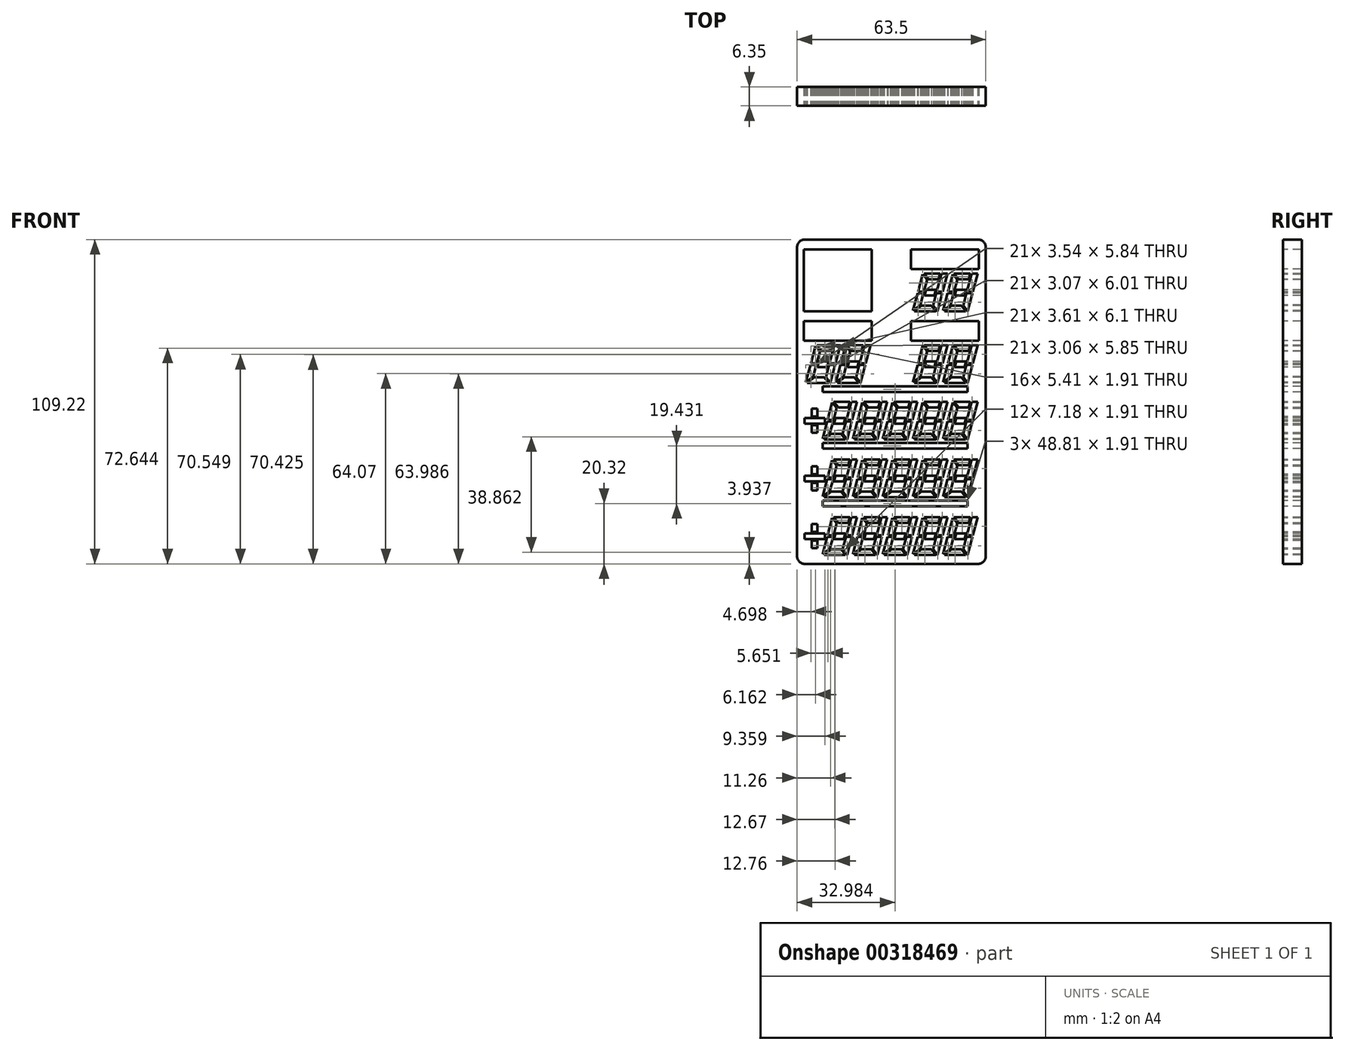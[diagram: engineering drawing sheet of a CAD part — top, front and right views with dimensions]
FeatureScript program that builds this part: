
annotation { "Feature Type Name" : "Feature", "Feature Type Description" : "" }
export const myFeature = defineFeature(function(context is Context, id is Id, definition is map)
    precondition{}
    {
        {
            var Q0;
            Q0=qCreatedBy(makeId("Front.planeOp"),FACE);
            var sketch = newSketch(context, id + "F0", { "sketchPlane" : qUnion([Q0])});
            skLineSegment(sketch, "E0.bottom", {"start": v(31.75, -54.61) * mm, "end": v(-31.75, -54.61) * mm});
            skLineSegment(sketch, "E0.top", {"start": v(31.75, 54.61) * mm, "end": v(-31.75, 54.6) * mm});
            skLineSegment(sketch, "E0.left", {"start": v(31.75, -54.61) * mm, "end": v(31.75, 54.61) * mm});
            skLineSegment(sketch, "E0.right", {"start": v(-31.75, -54.61) * mm, "end": v(-31.75, 54.6) * mm});
            skPoint(sketch, "E0.middle", {"position": v(0, 0) * mm});
            skSolve(sketch);
        }
        {
            var Q0;
            Q0=qSketchRegion(id+"F0",true);
            extrude(context, id + "F1", {"entities" : qUnion([Q0]), "depth" : 6.35 * mm, "offsetDistance" : 25.4 * mm});
        }
        {
            var Q0;
            Q0=makeQuery(id+"F1.opExtrude","CAP_FACE",FACE,{"disambiguationData":[OSD([sQuery(id+"F0.wireOp",EDGE,"E0.bottom"),sQuery(id+"F0.wireOp",EDGE,"E0.top"),sQuery(id+"F0.wireOp",EDGE,"E0.left"),sQuery(id+"F0.wireOp",EDGE,"E0.right")])],"isStart":false});
            var sketch = newSketch(context, id + "F2", { "sketchPlane" : qUnion([Q0])});
            skLineSegment(sketch, "E1", {"start": v(21.11, -38.93) * mm, "end": v(26.52, -38.93) * mm});
            skLineSegment(sketch, "E2", {"start": v(26.52, -38.93) * mm, "end": v(26.01, -40.83) * mm});
            skLineSegment(sketch, "E3", {"start": v(26.01, -40.83) * mm, "end": v(22.7, -40.83) * mm});
            skLineSegment(sketch, "E4", {"start": v(22.7, -40.83) * mm, "end": v(21.11, -38.93) * mm});
            skLineSegment(sketch, "E5", {"start": v(27.05, -38.93) * mm, "end": v(29.02, -38.93) * mm});
            skLineSegment(sketch, "E6", {"start": v(29.02, -38.93) * mm, "end": v(27.39, -45.02) * mm});
            skLineSegment(sketch, "E7", {"start": v(27.05, -38.93) * mm, "end": v(25.41, -45.02) * mm});
            skLineSegment(sketch, "E8", {"start": v(25.41, -45.02) * mm, "end": v(27.39, -45.02) * mm});
            skLineSegment(sketch, "E9", {"start": v(25.28, -45.53) * mm, "end": v(27.25, -45.53) * mm});
            skLineSegment(sketch, "E10", {"start": v(27.25, -45.53) * mm, "end": v(25.64, -51.54) * mm});
            skLineSegment(sketch, "E11", {"start": v(20.65, -39.17) * mm, "end": v(22.15, -40.95) * mm});
            skLineSegment(sketch, "E12", {"start": v(22.15, -40.95) * mm, "end": v(21.06, -45.02) * mm});
            skLineSegment(sketch, "E13", {"start": v(21.06, -45.02) * mm, "end": v(19.09, -45.02) * mm});
            skLineSegment(sketch, "E14", {"start": v(19.09, -45.02) * mm, "end": v(20.65, -39.17) * mm});
            skLineSegment(sketch, "E15", {"start": v(25.28, -45.53) * mm, "end": v(24.18, -49.61) * mm});
            skLineSegment(sketch, "E16", {"start": v(24.18, -49.61) * mm, "end": v(25.64, -51.54) * mm});
            skLineSegment(sketch, "E17", {"start": v(25.06, -51.63) * mm, "end": v(23.63, -49.72) * mm});
            skLineSegment(sketch, "E18", {"start": v(23.63, -49.72) * mm, "end": v(20.33, -49.72) * mm});
            skLineSegment(sketch, "E19", {"start": v(25.06, -51.63) * mm, "end": v(17.89, -51.63) * mm});
            skLineSegment(sketch, "E20", {"start": v(17.89, -51.63) * mm, "end": v(20.33, -49.72) * mm});
            skLineSegment(sketch, "E21", {"start": v(20.92, -45.53) * mm, "end": v(18.95, -45.53) * mm});
            skLineSegment(sketch, "E22", {"start": v(18.95, -45.53) * mm, "end": v(17.39, -51.37) * mm});
            skLineSegment(sketch, "E23", {"start": v(17.39, -51.37) * mm, "end": v(19.88, -49.42) * mm});
            skLineSegment(sketch, "E24", {"start": v(19.88, -49.42) * mm, "end": v(20.92, -45.53) * mm});
            skLineSegment(sketch, "E25", {"start": v(21.77, -44.32) * mm, "end": v(21.26, -46.23) * mm});
            skLineSegment(sketch, "E26", {"start": v(21.26, -46.23) * mm, "end": v(24.56, -46.23) * mm});
            skLineSegment(sketch, "E27", {"start": v(24.56, -46.23) * mm, "end": v(25.08, -44.32) * mm});
            skLineSegment(sketch, "E28", {"start": v(25.08, -44.32) * mm, "end": v(21.77, -44.32) * mm});
            skLineSegment(sketch, "E29.0.1.0", {"start": v(21.26, -26.8) * mm, "end": v(24.56, -26.8) * mm});
            skLineSegment(sketch, "E29.0.1.1", {"start": v(18.95, -26.1) * mm, "end": v(17.39, -31.94) * mm});
            skLineSegment(sketch, "E29.0.1.2", {"start": v(22.15, -21.52) * mm, "end": v(21.06, -25.6) * mm});
            skLineSegment(sketch, "E29.0.1.3", {"start": v(29.02, -19.5) * mm, "end": v(27.39, -25.6) * mm});
            skLineSegment(sketch, "E29.0.1.4", {"start": v(26.01, -21.4) * mm, "end": v(22.7, -21.4) * mm});
            skLineSegment(sketch, "E29.0.1.5", {"start": v(25.06, -32.2) * mm, "end": v(17.89, -32.2) * mm});
            skLineSegment(sketch, "E29.0.1.6", {"start": v(27.05, -19.5) * mm, "end": v(25.41, -25.6) * mm});
            skLineSegment(sketch, "E29.0.1.7", {"start": v(23.63, -30.29) * mm, "end": v(20.33, -30.29) * mm});
            skLineSegment(sketch, "E29.0.1.8", {"start": v(25.08, -24.9) * mm, "end": v(21.77, -24.9) * mm});
            skLineSegment(sketch, "E29.0.1.9", {"start": v(25.28, -26.1) * mm, "end": v(24.18, -30.18) * mm});
            skLineSegment(sketch, "E29.0.1.10", {"start": v(27.25, -26.1) * mm, "end": v(25.64, -32.11) * mm});
            skLineSegment(sketch, "E29.0.1.11", {"start": v(19.09, -25.6) * mm, "end": v(20.65, -19.74) * mm});
            skLineSegment(sketch, "E29.0.1.12", {"start": v(21.11, -19.5) * mm, "end": v(26.52, -19.5) * mm});
            skLineSegment(sketch, "E29.0.1.13", {"start": v(20.65, -19.74) * mm, "end": v(22.15, -21.52) * mm});
            skLineSegment(sketch, "E29.0.1.14", {"start": v(21.06, -25.6) * mm, "end": v(19.09, -25.6) * mm});
            skLineSegment(sketch, "E29.0.1.15", {"start": v(19.88, -30) * mm, "end": v(20.92, -26.1) * mm});
            skLineSegment(sketch, "E29.0.1.16", {"start": v(22.7, -21.4) * mm, "end": v(21.11, -19.5) * mm});
            skLineSegment(sketch, "E29.0.1.17", {"start": v(17.89, -32.2) * mm, "end": v(20.33, -30.29) * mm});
            skLineSegment(sketch, "E29.0.1.18", {"start": v(27.05, -19.5) * mm, "end": v(29.02, -19.5) * mm});
            skLineSegment(sketch, "E29.0.1.19", {"start": v(20.92, -26.1) * mm, "end": v(18.95, -26.1) * mm});
            skLineSegment(sketch, "E29.0.1.20", {"start": v(17.39, -31.94) * mm, "end": v(19.88, -30) * mm});
            skLineSegment(sketch, "E29.0.1.21", {"start": v(25.06, -32.2) * mm, "end": v(23.63, -30.29) * mm});
            skLineSegment(sketch, "E29.0.1.22", {"start": v(26.52, -19.5) * mm, "end": v(26.01, -21.4) * mm});
            skLineSegment(sketch, "E29.0.1.23", {"start": v(24.18, -30.18) * mm, "end": v(25.64, -32.11) * mm});
            skLineSegment(sketch, "E29.0.1.24", {"start": v(21.77, -24.9) * mm, "end": v(21.26, -26.8) * mm});
            skLineSegment(sketch, "E29.0.1.25", {"start": v(25.28, -26.1) * mm, "end": v(27.25, -26.1) * mm});
            skLineSegment(sketch, "E29.0.1.26", {"start": v(25.41, -25.6) * mm, "end": v(27.39, -25.6) * mm});
            skLineSegment(sketch, "E29.0.1.27", {"start": v(24.56, -26.8) * mm, "end": v(25.08, -24.9) * mm});
            skLineSegment(sketch, "E29.0.2.0", {"start": v(21.26, -7.37) * mm, "end": v(24.56, -7.37) * mm});
            skLineSegment(sketch, "E29.0.2.1", {"start": v(18.95, -6.67) * mm, "end": v(17.39, -12.51) * mm});
            skLineSegment(sketch, "E29.0.2.2", {"start": v(22.15, -2.1) * mm, "end": v(21.06, -6.16) * mm});
            skLineSegment(sketch, "E29.0.2.3", {"start": v(29.02, -0.06) * mm, "end": v(27.39, -6.16) * mm});
            skLineSegment(sketch, "E29.0.2.4", {"start": v(26.01, -1.97) * mm, "end": v(22.7, -1.97) * mm});
            skLineSegment(sketch, "E29.0.2.5", {"start": v(25.06, -12.76) * mm, "end": v(17.89, -12.76) * mm});
            skLineSegment(sketch, "E29.0.2.6", {"start": v(27.05, -0.06) * mm, "end": v(25.41, -6.16) * mm});
            skLineSegment(sketch, "E29.0.2.7", {"start": v(23.63, -10.86) * mm, "end": v(20.33, -10.86) * mm});
            skLineSegment(sketch, "E29.0.2.8", {"start": v(25.08, -5.46) * mm, "end": v(21.77, -5.46) * mm});
            skLineSegment(sketch, "E29.0.2.9", {"start": v(25.28, -6.67) * mm, "end": v(24.18, -10.75) * mm});
            skLineSegment(sketch, "E29.0.2.10", {"start": v(27.25, -6.67) * mm, "end": v(25.64, -12.68) * mm});
            skLineSegment(sketch, "E29.0.2.11", {"start": v(19.09, -6.16) * mm, "end": v(20.65, -0.31) * mm});
            skLineSegment(sketch, "E29.0.2.12", {"start": v(21.11, -0.06) * mm, "end": v(26.52, -0.06) * mm});
            skLineSegment(sketch, "E29.0.2.13", {"start": v(20.65, -0.31) * mm, "end": v(22.15, -2.1) * mm});
            skLineSegment(sketch, "E29.0.2.14", {"start": v(21.06, -6.16) * mm, "end": v(19.09, -6.16) * mm});
            skLineSegment(sketch, "E29.0.2.15", {"start": v(19.88, -10.56) * mm, "end": v(20.92, -6.67) * mm});
            skLineSegment(sketch, "E29.0.2.16", {"start": v(22.7, -1.97) * mm, "end": v(21.11, -0.06) * mm});
            skLineSegment(sketch, "E29.0.2.17", {"start": v(17.89, -12.76) * mm, "end": v(20.33, -10.86) * mm});
            skLineSegment(sketch, "E29.0.2.18", {"start": v(27.05, -0.06) * mm, "end": v(29.02, -0.06) * mm});
            skLineSegment(sketch, "E29.0.2.19", {"start": v(20.92, -6.67) * mm, "end": v(18.95, -6.67) * mm});
            skLineSegment(sketch, "E29.0.2.20", {"start": v(17.39, -12.51) * mm, "end": v(19.88, -10.56) * mm});
            skLineSegment(sketch, "E29.0.2.21", {"start": v(25.06, -12.76) * mm, "end": v(23.63, -10.86) * mm});
            skLineSegment(sketch, "E29.0.2.22", {"start": v(26.52, -0.06) * mm, "end": v(26.01, -1.97) * mm});
            skLineSegment(sketch, "E29.0.2.23", {"start": v(24.18, -10.75) * mm, "end": v(25.64, -12.68) * mm});
            skLineSegment(sketch, "E29.0.2.24", {"start": v(21.77, -5.46) * mm, "end": v(21.26, -7.37) * mm});
            skLineSegment(sketch, "E29.0.2.25", {"start": v(25.28, -6.67) * mm, "end": v(27.25, -6.67) * mm});
            skLineSegment(sketch, "E29.0.2.26", {"start": v(25.41, -6.16) * mm, "end": v(27.39, -6.16) * mm});
            skLineSegment(sketch, "E29.0.2.27", {"start": v(24.56, -7.37) * mm, "end": v(25.08, -5.46) * mm});
            skLineSegment(sketch, "E29.1.0.0", {"start": v(11.12, -46.23) * mm, "end": v(14.43, -46.23) * mm});
            skLineSegment(sketch, "E29.1.0.1", {"start": v(8.81, -45.53) * mm, "end": v(7.25, -51.37) * mm});
            skLineSegment(sketch, "E29.1.0.2", {"start": v(12.01, -40.95) * mm, "end": v(10.92, -45.02) * mm});
            skLineSegment(sketch, "E29.1.0.3", {"start": v(18.88, -38.93) * mm, "end": v(17.25, -45.02) * mm});
            skLineSegment(sketch, "E29.1.0.4", {"start": v(15.87, -40.83) * mm, "end": v(12.57, -40.83) * mm});
            skLineSegment(sketch, "E29.1.0.5", {"start": v(14.93, -51.63) * mm, "end": v(7.75, -51.63) * mm});
            skLineSegment(sketch, "E29.1.0.6", {"start": v(16.9, -38.93) * mm, "end": v(15.27, -45.02) * mm});
            skLineSegment(sketch, "E29.1.0.7", {"start": v(13.49, -49.72) * mm, "end": v(10.19, -49.72) * mm});
            skLineSegment(sketch, "E29.1.0.8", {"start": v(14.94, -44.32) * mm, "end": v(11.63, -44.32) * mm});
            skLineSegment(sketch, "E29.1.0.9", {"start": v(15.14, -45.53) * mm, "end": v(14.04, -49.61) * mm});
            skLineSegment(sketch, "E29.1.0.10", {"start": v(17.11, -45.53) * mm, "end": v(15.5, -51.54) * mm});
            skLineSegment(sketch, "E29.1.0.11", {"start": v(8.95, -45.02) * mm, "end": v(10.52, -39.17) * mm});
            skLineSegment(sketch, "E29.1.0.12", {"start": v(10.97, -38.93) * mm, "end": v(16.38, -38.93) * mm});
            skLineSegment(sketch, "E29.1.0.13", {"start": v(10.52, -39.17) * mm, "end": v(12.01, -40.95) * mm});
            skLineSegment(sketch, "E29.1.0.14", {"start": v(10.92, -45.02) * mm, "end": v(8.95, -45.02) * mm});
            skLineSegment(sketch, "E29.1.0.15", {"start": v(9.74, -49.42) * mm, "end": v(10.78, -45.53) * mm});
            skLineSegment(sketch, "E29.1.0.16", {"start": v(12.57, -40.83) * mm, "end": v(10.97, -38.93) * mm});
            skLineSegment(sketch, "E29.1.0.17", {"start": v(7.75, -51.63) * mm, "end": v(10.19, -49.72) * mm});
            skLineSegment(sketch, "E29.1.0.18", {"start": v(16.9, -38.93) * mm, "end": v(18.88, -38.93) * mm});
            skLineSegment(sketch, "E29.1.0.19", {"start": v(10.78, -45.53) * mm, "end": v(8.81, -45.53) * mm});
            skLineSegment(sketch, "E29.1.0.20", {"start": v(7.25, -51.37) * mm, "end": v(9.74, -49.42) * mm});
            skLineSegment(sketch, "E29.1.0.21", {"start": v(14.93, -51.63) * mm, "end": v(13.49, -49.72) * mm});
            skLineSegment(sketch, "E29.1.0.22", {"start": v(16.38, -38.93) * mm, "end": v(15.87, -40.83) * mm});
            skLineSegment(sketch, "E29.1.0.23", {"start": v(14.04, -49.61) * mm, "end": v(15.5, -51.54) * mm});
            skLineSegment(sketch, "E29.1.0.24", {"start": v(11.63, -44.32) * mm, "end": v(11.12, -46.23) * mm});
            skLineSegment(sketch, "E29.1.0.25", {"start": v(15.14, -45.53) * mm, "end": v(17.11, -45.53) * mm});
            skLineSegment(sketch, "E29.1.0.26", {"start": v(15.27, -45.02) * mm, "end": v(17.25, -45.02) * mm});
            skLineSegment(sketch, "E29.1.0.27", {"start": v(14.43, -46.23) * mm, "end": v(14.94, -44.32) * mm});
            skLineSegment(sketch, "E29.1.1.0", {"start": v(11.12, -26.8) * mm, "end": v(14.43, -26.8) * mm});
            skLineSegment(sketch, "E29.1.1.1", {"start": v(8.81, -26.1) * mm, "end": v(7.25, -31.94) * mm});
            skLineSegment(sketch, "E29.1.1.2", {"start": v(12.01, -21.52) * mm, "end": v(10.92, -25.6) * mm});
            skLineSegment(sketch, "E29.1.1.3", {"start": v(18.88, -19.5) * mm, "end": v(17.25, -25.6) * mm});
            skLineSegment(sketch, "E29.1.1.4", {"start": v(15.87, -21.4) * mm, "end": v(12.57, -21.4) * mm});
            skLineSegment(sketch, "E29.1.1.5", {"start": v(14.93, -32.2) * mm, "end": v(7.75, -32.2) * mm});
            skLineSegment(sketch, "E29.1.1.6", {"start": v(16.9, -19.5) * mm, "end": v(15.27, -25.6) * mm});
            skLineSegment(sketch, "E29.1.1.7", {"start": v(13.49, -30.29) * mm, "end": v(10.19, -30.29) * mm});
            skLineSegment(sketch, "E29.1.1.8", {"start": v(14.94, -24.9) * mm, "end": v(11.63, -24.9) * mm});
            skLineSegment(sketch, "E29.1.1.9", {"start": v(15.14, -26.1) * mm, "end": v(14.04, -30.18) * mm});
            skLineSegment(sketch, "E29.1.1.10", {"start": v(17.11, -26.1) * mm, "end": v(15.5, -32.11) * mm});
            skLineSegment(sketch, "E29.1.1.11", {"start": v(8.95, -25.6) * mm, "end": v(10.52, -19.74) * mm});
            skLineSegment(sketch, "E29.1.1.12", {"start": v(10.97, -19.5) * mm, "end": v(16.38, -19.5) * mm});
            skLineSegment(sketch, "E29.1.1.13", {"start": v(10.52, -19.74) * mm, "end": v(12.01, -21.52) * mm});
            skLineSegment(sketch, "E29.1.1.14", {"start": v(10.92, -25.6) * mm, "end": v(8.95, -25.6) * mm});
            skLineSegment(sketch, "E29.1.1.15", {"start": v(9.74, -30) * mm, "end": v(10.78, -26.1) * mm});
            skLineSegment(sketch, "E29.1.1.16", {"start": v(12.57, -21.4) * mm, "end": v(10.97, -19.5) * mm});
            skLineSegment(sketch, "E29.1.1.17", {"start": v(7.75, -32.2) * mm, "end": v(10.19, -30.29) * mm});
            skLineSegment(sketch, "E29.1.1.18", {"start": v(16.9, -19.5) * mm, "end": v(18.88, -19.5) * mm});
            skLineSegment(sketch, "E29.1.1.19", {"start": v(10.78, -26.1) * mm, "end": v(8.81, -26.1) * mm});
            skLineSegment(sketch, "E29.1.1.20", {"start": v(7.25, -31.94) * mm, "end": v(9.74, -30) * mm});
            skLineSegment(sketch, "E29.1.1.21", {"start": v(14.93, -32.2) * mm, "end": v(13.49, -30.29) * mm});
            skLineSegment(sketch, "E29.1.1.22", {"start": v(16.38, -19.5) * mm, "end": v(15.87, -21.4) * mm});
            skLineSegment(sketch, "E29.1.1.23", {"start": v(14.04, -30.18) * mm, "end": v(15.5, -32.11) * mm});
            skLineSegment(sketch, "E29.1.1.24", {"start": v(11.63, -24.9) * mm, "end": v(11.12, -26.8) * mm});
            skLineSegment(sketch, "E29.1.1.25", {"start": v(15.14, -26.1) * mm, "end": v(17.11, -26.1) * mm});
            skLineSegment(sketch, "E29.1.1.26", {"start": v(15.27, -25.6) * mm, "end": v(17.25, -25.6) * mm});
            skLineSegment(sketch, "E29.1.1.27", {"start": v(14.43, -26.8) * mm, "end": v(14.94, -24.9) * mm});
            skLineSegment(sketch, "E29.1.2.0", {"start": v(11.12, -7.37) * mm, "end": v(14.43, -7.37) * mm});
            skLineSegment(sketch, "E29.1.2.1", {"start": v(8.81, -6.67) * mm, "end": v(7.25, -12.51) * mm});
            skLineSegment(sketch, "E29.1.2.2", {"start": v(12.01, -2.1) * mm, "end": v(10.92, -6.16) * mm});
            skLineSegment(sketch, "E29.1.2.3", {"start": v(18.88, -0.06) * mm, "end": v(17.25, -6.16) * mm});
            skLineSegment(sketch, "E29.1.2.4", {"start": v(15.87, -1.97) * mm, "end": v(12.57, -1.97) * mm});
            skLineSegment(sketch, "E29.1.2.5", {"start": v(14.93, -12.76) * mm, "end": v(7.75, -12.76) * mm});
            skLineSegment(sketch, "E29.1.2.6", {"start": v(16.9, -0.06) * mm, "end": v(15.27, -6.16) * mm});
            skLineSegment(sketch, "E29.1.2.7", {"start": v(13.49, -10.86) * mm, "end": v(10.19, -10.86) * mm});
            skLineSegment(sketch, "E29.1.2.8", {"start": v(14.94, -5.46) * mm, "end": v(11.63, -5.46) * mm});
            skLineSegment(sketch, "E29.1.2.9", {"start": v(15.14, -6.67) * mm, "end": v(14.04, -10.75) * mm});
            skLineSegment(sketch, "E29.1.2.10", {"start": v(17.11, -6.67) * mm, "end": v(15.5, -12.68) * mm});
            skLineSegment(sketch, "E29.1.2.11", {"start": v(8.95, -6.16) * mm, "end": v(10.52, -0.31) * mm});
            skLineSegment(sketch, "E29.1.2.12", {"start": v(10.97, -0.06) * mm, "end": v(16.38, -0.06) * mm});
            skLineSegment(sketch, "E29.1.2.13", {"start": v(10.52, -0.31) * mm, "end": v(12.01, -2.1) * mm});
            skLineSegment(sketch, "E29.1.2.14", {"start": v(10.92, -6.16) * mm, "end": v(8.95, -6.16) * mm});
            skLineSegment(sketch, "E29.1.2.15", {"start": v(9.74, -10.56) * mm, "end": v(10.78, -6.67) * mm});
            skLineSegment(sketch, "E29.1.2.16", {"start": v(12.57, -1.97) * mm, "end": v(10.97, -0.06) * mm});
            skLineSegment(sketch, "E29.1.2.17", {"start": v(7.75, -12.76) * mm, "end": v(10.19, -10.86) * mm});
            skLineSegment(sketch, "E29.1.2.18", {"start": v(16.9, -0.06) * mm, "end": v(18.88, -0.06) * mm});
            skLineSegment(sketch, "E29.1.2.19", {"start": v(10.78, -6.67) * mm, "end": v(8.81, -6.67) * mm});
            skLineSegment(sketch, "E29.1.2.20", {"start": v(7.25, -12.51) * mm, "end": v(9.74, -10.56) * mm});
            skLineSegment(sketch, "E29.1.2.21", {"start": v(14.93, -12.76) * mm, "end": v(13.49, -10.86) * mm});
            skLineSegment(sketch, "E29.1.2.22", {"start": v(16.38, -0.06) * mm, "end": v(15.87, -1.97) * mm});
            skLineSegment(sketch, "E29.1.2.23", {"start": v(14.04, -10.75) * mm, "end": v(15.5, -12.68) * mm});
            skLineSegment(sketch, "E29.1.2.24", {"start": v(11.63, -5.46) * mm, "end": v(11.12, -7.37) * mm});
            skLineSegment(sketch, "E29.1.2.25", {"start": v(15.14, -6.67) * mm, "end": v(17.11, -6.67) * mm});
            skLineSegment(sketch, "E29.1.2.26", {"start": v(15.27, -6.16) * mm, "end": v(17.25, -6.16) * mm});
            skLineSegment(sketch, "E29.1.2.27", {"start": v(14.43, -7.37) * mm, "end": v(14.94, -5.46) * mm});
            skLineSegment(sketch, "E29.2.0.0", {"start": v(0.98, -46.23) * mm, "end": v(4.29, -46.23) * mm});
            skLineSegment(sketch, "E29.2.0.1", {"start": v(-1.33, -45.53) * mm, "end": v(-2.9, -51.37) * mm});
            skLineSegment(sketch, "E29.2.0.2", {"start": v(1.87, -40.95) * mm, "end": v(0.78, -45.02) * mm});
            skLineSegment(sketch, "E29.2.0.3", {"start": v(8.74, -38.93) * mm, "end": v(7.1, -45.02) * mm});
            skLineSegment(sketch, "E29.2.0.4", {"start": v(5.73, -40.83) * mm, "end": v(2.43, -40.83) * mm});
            skLineSegment(sketch, "E29.2.0.5", {"start": v(4.79, -51.63) * mm, "end": v(-2.39, -51.63) * mm});
            skLineSegment(sketch, "E29.2.0.6", {"start": v(6.77, -38.93) * mm, "end": v(5.14, -45.02) * mm});
            skLineSegment(sketch, "E29.2.0.7", {"start": v(3.35, -49.72) * mm, "end": v(0.05, -49.72) * mm});
            skLineSegment(sketch, "E29.2.0.8", {"start": v(4.8, -44.32) * mm, "end": v(1.5, -44.32) * mm});
            skLineSegment(sketch, "E29.2.0.9", {"start": v(5, -45.53) * mm, "end": v(3.9, -49.61) * mm});
            skLineSegment(sketch, "E29.2.0.10", {"start": v(6.97, -45.53) * mm, "end": v(5.36, -51.54) * mm});
            skLineSegment(sketch, "E29.2.0.11", {"start": v(-1.2, -45.02) * mm, "end": v(0.38, -39.17) * mm});
            skLineSegment(sketch, "E29.2.0.12", {"start": v(0.83, -38.93) * mm, "end": v(6.24, -38.93) * mm});
            skLineSegment(sketch, "E29.2.0.13", {"start": v(0.38, -39.17) * mm, "end": v(1.87, -40.95) * mm});
            skLineSegment(sketch, "E29.2.0.14", {"start": v(0.78, -45.02) * mm, "end": v(-1.2, -45.02) * mm});
            skLineSegment(sketch, "E29.2.0.15", {"start": v(-0.4, -49.42) * mm, "end": v(0.65, -45.53) * mm});
            skLineSegment(sketch, "E29.2.0.16", {"start": v(2.43, -40.83) * mm, "end": v(0.83, -38.93) * mm});
            skLineSegment(sketch, "E29.2.0.17", {"start": v(-2.39, -51.63) * mm, "end": v(0.05, -49.72) * mm});
            skLineSegment(sketch, "E29.2.0.18", {"start": v(6.77, -38.93) * mm, "end": v(8.74, -38.93) * mm});
            skLineSegment(sketch, "E29.2.0.19", {"start": v(0.65, -45.53) * mm, "end": v(-1.33, -45.53) * mm});
            skLineSegment(sketch, "E29.2.0.20", {"start": v(-2.9, -51.37) * mm, "end": v(-0.4, -49.42) * mm});
            skLineSegment(sketch, "E29.2.0.21", {"start": v(4.79, -51.63) * mm, "end": v(3.35, -49.72) * mm});
            skLineSegment(sketch, "E29.2.0.22", {"start": v(6.24, -38.93) * mm, "end": v(5.73, -40.83) * mm});
            skLineSegment(sketch, "E29.2.0.23", {"start": v(3.9, -49.61) * mm, "end": v(5.36, -51.54) * mm});
            skLineSegment(sketch, "E29.2.0.24", {"start": v(1.5, -44.32) * mm, "end": v(0.98, -46.23) * mm});
            skLineSegment(sketch, "E29.2.0.25", {"start": v(5, -45.53) * mm, "end": v(6.97, -45.53) * mm});
            skLineSegment(sketch, "E29.2.0.26", {"start": v(5.14, -45.02) * mm, "end": v(7.1, -45.02) * mm});
            skLineSegment(sketch, "E29.2.0.27", {"start": v(4.29, -46.23) * mm, "end": v(4.8, -44.32) * mm});
            skLineSegment(sketch, "E29.2.1.0", {"start": v(0.98, -26.8) * mm, "end": v(4.29, -26.8) * mm});
            skLineSegment(sketch, "E29.2.1.1", {"start": v(-1.33, -26.1) * mm, "end": v(-2.9, -31.94) * mm});
            skLineSegment(sketch, "E29.2.1.2", {"start": v(1.87, -21.52) * mm, "end": v(0.78, -25.6) * mm});
            skLineSegment(sketch, "E29.2.1.3", {"start": v(8.74, -19.5) * mm, "end": v(7.1, -25.6) * mm});
            skLineSegment(sketch, "E29.2.1.4", {"start": v(5.73, -21.4) * mm, "end": v(2.43, -21.4) * mm});
            skLineSegment(sketch, "E29.2.1.5", {"start": v(4.79, -32.2) * mm, "end": v(-2.39, -32.2) * mm});
            skLineSegment(sketch, "E29.2.1.6", {"start": v(6.77, -19.5) * mm, "end": v(5.14, -25.6) * mm});
            skLineSegment(sketch, "E29.2.1.7", {"start": v(3.35, -30.29) * mm, "end": v(0.05, -30.29) * mm});
            skLineSegment(sketch, "E29.2.1.8", {"start": v(4.8, -24.9) * mm, "end": v(1.5, -24.9) * mm});
            skLineSegment(sketch, "E29.2.1.9", {"start": v(5, -26.1) * mm, "end": v(3.9, -30.18) * mm});
            skLineSegment(sketch, "E29.2.1.10", {"start": v(6.97, -26.1) * mm, "end": v(5.36, -32.11) * mm});
            skLineSegment(sketch, "E29.2.1.11", {"start": v(-1.2, -25.6) * mm, "end": v(0.38, -19.74) * mm});
            skLineSegment(sketch, "E29.2.1.12", {"start": v(0.83, -19.5) * mm, "end": v(6.24, -19.5) * mm});
            skLineSegment(sketch, "E29.2.1.13", {"start": v(0.38, -19.74) * mm, "end": v(1.87, -21.52) * mm});
            skLineSegment(sketch, "E29.2.1.14", {"start": v(0.78, -25.6) * mm, "end": v(-1.2, -25.6) * mm});
            skLineSegment(sketch, "E29.2.1.15", {"start": v(-0.4, -30) * mm, "end": v(0.65, -26.1) * mm});
            skLineSegment(sketch, "E29.2.1.16", {"start": v(2.43, -21.4) * mm, "end": v(0.83, -19.5) * mm});
            skLineSegment(sketch, "E29.2.1.17", {"start": v(-2.39, -32.2) * mm, "end": v(0.05, -30.29) * mm});
            skLineSegment(sketch, "E29.2.1.18", {"start": v(6.77, -19.5) * mm, "end": v(8.74, -19.5) * mm});
            skLineSegment(sketch, "E29.2.1.19", {"start": v(0.65, -26.1) * mm, "end": v(-1.33, -26.1) * mm});
            skLineSegment(sketch, "E29.2.1.20", {"start": v(-2.9, -31.94) * mm, "end": v(-0.4, -30) * mm});
            skLineSegment(sketch, "E29.2.1.21", {"start": v(4.79, -32.2) * mm, "end": v(3.35, -30.29) * mm});
            skLineSegment(sketch, "E29.2.1.22", {"start": v(6.24, -19.5) * mm, "end": v(5.73, -21.4) * mm});
            skLineSegment(sketch, "E29.2.1.23", {"start": v(3.9, -30.18) * mm, "end": v(5.36, -32.11) * mm});
            skLineSegment(sketch, "E29.2.1.24", {"start": v(1.5, -24.9) * mm, "end": v(0.98, -26.8) * mm});
            skLineSegment(sketch, "E29.2.1.25", {"start": v(5, -26.1) * mm, "end": v(6.97, -26.1) * mm});
            skLineSegment(sketch, "E29.2.1.26", {"start": v(5.14, -25.6) * mm, "end": v(7.1, -25.6) * mm});
            skLineSegment(sketch, "E29.2.1.27", {"start": v(4.29, -26.8) * mm, "end": v(4.8, -24.9) * mm});
            skLineSegment(sketch, "E29.2.2.0", {"start": v(0.98, -7.37) * mm, "end": v(4.29, -7.37) * mm});
            skLineSegment(sketch, "E29.2.2.1", {"start": v(-1.33, -6.67) * mm, "end": v(-2.9, -12.51) * mm});
            skLineSegment(sketch, "E29.2.2.2", {"start": v(1.87, -2.1) * mm, "end": v(0.78, -6.16) * mm});
            skLineSegment(sketch, "E29.2.2.3", {"start": v(8.74, -0.06) * mm, "end": v(7.1, -6.16) * mm});
            skLineSegment(sketch, "E29.2.2.4", {"start": v(5.73, -1.97) * mm, "end": v(2.43, -1.97) * mm});
            skLineSegment(sketch, "E29.2.2.5", {"start": v(4.79, -12.76) * mm, "end": v(-2.39, -12.76) * mm});
            skLineSegment(sketch, "E29.2.2.6", {"start": v(6.77, -0.06) * mm, "end": v(5.14, -6.16) * mm});
            skLineSegment(sketch, "E29.2.2.7", {"start": v(3.35, -10.86) * mm, "end": v(0.05, -10.86) * mm});
            skLineSegment(sketch, "E29.2.2.8", {"start": v(4.8, -5.46) * mm, "end": v(1.5, -5.46) * mm});
            skLineSegment(sketch, "E29.2.2.9", {"start": v(5, -6.67) * mm, "end": v(3.9, -10.75) * mm});
            skLineSegment(sketch, "E29.2.2.10", {"start": v(6.97, -6.67) * mm, "end": v(5.36, -12.68) * mm});
            skLineSegment(sketch, "E29.2.2.11", {"start": v(-1.2, -6.16) * mm, "end": v(0.38, -0.31) * mm});
            skLineSegment(sketch, "E29.2.2.12", {"start": v(0.83, -0.06) * mm, "end": v(6.24, -0.06) * mm});
            skLineSegment(sketch, "E29.2.2.13", {"start": v(0.38, -0.31) * mm, "end": v(1.87, -2.1) * mm});
            skLineSegment(sketch, "E29.2.2.14", {"start": v(0.78, -6.16) * mm, "end": v(-1.2, -6.16) * mm});
            skLineSegment(sketch, "E29.2.2.15", {"start": v(-0.4, -10.56) * mm, "end": v(0.65, -6.67) * mm});
            skLineSegment(sketch, "E29.2.2.16", {"start": v(2.43, -1.97) * mm, "end": v(0.83, -0.06) * mm});
            skLineSegment(sketch, "E29.2.2.17", {"start": v(-2.39, -12.76) * mm, "end": v(0.05, -10.86) * mm});
            skLineSegment(sketch, "E29.2.2.18", {"start": v(6.77, -0.06) * mm, "end": v(8.74, -0.06) * mm});
            skLineSegment(sketch, "E29.2.2.19", {"start": v(0.65, -6.67) * mm, "end": v(-1.33, -6.67) * mm});
            skLineSegment(sketch, "E29.2.2.20", {"start": v(-2.9, -12.51) * mm, "end": v(-0.4, -10.56) * mm});
            skLineSegment(sketch, "E29.2.2.21", {"start": v(4.79, -12.76) * mm, "end": v(3.35, -10.86) * mm});
            skLineSegment(sketch, "E29.2.2.22", {"start": v(6.24, -0.06) * mm, "end": v(5.73, -1.97) * mm});
            skLineSegment(sketch, "E29.2.2.23", {"start": v(3.9, -10.75) * mm, "end": v(5.36, -12.68) * mm});
            skLineSegment(sketch, "E29.2.2.24", {"start": v(1.5, -5.46) * mm, "end": v(0.98, -7.37) * mm});
            skLineSegment(sketch, "E29.2.2.25", {"start": v(5, -6.67) * mm, "end": v(6.97, -6.67) * mm});
            skLineSegment(sketch, "E29.2.2.26", {"start": v(5.14, -6.16) * mm, "end": v(7.1, -6.16) * mm});
            skLineSegment(sketch, "E29.2.2.27", {"start": v(4.29, -7.37) * mm, "end": v(4.8, -5.46) * mm});
            skLineSegment(sketch, "E29.3.0.0", {"start": v(-9.15, -46.23) * mm, "end": v(-5.85, -46.23) * mm});
            skLineSegment(sketch, "E29.3.0.1", {"start": v(-11.47, -45.53) * mm, "end": v(-13.03, -51.37) * mm});
            skLineSegment(sketch, "E29.3.0.2", {"start": v(-8.27, -40.95) * mm, "end": v(-9.36, -45.02) * mm});
            skLineSegment(sketch, "E29.3.0.3", {"start": v(-1.4, -38.93) * mm, "end": v(-3.03, -45.02) * mm});
            skLineSegment(sketch, "E29.3.0.4", {"start": v(-4.4, -40.83) * mm, "end": v(-7.7, -40.83) * mm});
            skLineSegment(sketch, "E29.3.0.5", {"start": v(-5.35, -51.63) * mm, "end": v(-12.53, -51.63) * mm});
            skLineSegment(sketch, "E29.3.0.6", {"start": v(-3.37, -38.93) * mm, "end": v(-5, -45.02) * mm});
            skLineSegment(sketch, "E29.3.0.7", {"start": v(-6.79, -49.72) * mm, "end": v(-10.1, -49.72) * mm});
            skLineSegment(sketch, "E29.3.0.8", {"start": v(-5.34, -44.32) * mm, "end": v(-8.64, -44.32) * mm});
            skLineSegment(sketch, "E29.3.0.9", {"start": v(-5.14, -45.53) * mm, "end": v(-6.23, -49.61) * mm});
            skLineSegment(sketch, "E29.3.0.10", {"start": v(-3.17, -45.53) * mm, "end": v(-4.78, -51.54) * mm});
            skLineSegment(sketch, "E29.3.0.11", {"start": v(-11.33, -45.02) * mm, "end": v(-9.76, -39.17) * mm});
            skLineSegment(sketch, "E29.3.0.12", {"start": v(-9.3, -38.93) * mm, "end": v(-3.9, -38.93) * mm});
            skLineSegment(sketch, "E29.3.0.13", {"start": v(-9.76, -39.17) * mm, "end": v(-8.27, -40.95) * mm});
            skLineSegment(sketch, "E29.3.0.14", {"start": v(-9.36, -45.02) * mm, "end": v(-11.33, -45.02) * mm});
            skLineSegment(sketch, "E29.3.0.15", {"start": v(-10.54, -49.42) * mm, "end": v(-9.5, -45.53) * mm});
            skLineSegment(sketch, "E29.3.0.16", {"start": v(-7.7, -40.83) * mm, "end": v(-9.3, -38.93) * mm});
            skLineSegment(sketch, "E29.3.0.17", {"start": v(-12.53, -51.63) * mm, "end": v(-10.1, -49.72) * mm});
            skLineSegment(sketch, "E29.3.0.18", {"start": v(-3.37, -38.93) * mm, "end": v(-1.4, -38.93) * mm});
            skLineSegment(sketch, "E29.3.0.19", {"start": v(-9.5, -45.53) * mm, "end": v(-11.47, -45.53) * mm});
            skLineSegment(sketch, "E29.3.0.20", {"start": v(-13.03, -51.37) * mm, "end": v(-10.54, -49.42) * mm});
            skLineSegment(sketch, "E29.3.0.21", {"start": v(-5.35, -51.63) * mm, "end": v(-6.79, -49.72) * mm});
            skLineSegment(sketch, "E29.3.0.22", {"start": v(-3.9, -38.93) * mm, "end": v(-4.4, -40.83) * mm});
            skLineSegment(sketch, "E29.3.0.23", {"start": v(-6.23, -49.61) * mm, "end": v(-4.78, -51.54) * mm});
            skLineSegment(sketch, "E29.3.0.24", {"start": v(-8.64, -44.32) * mm, "end": v(-9.15, -46.23) * mm});
            skLineSegment(sketch, "E29.3.0.25", {"start": v(-5.14, -45.53) * mm, "end": v(-3.17, -45.53) * mm});
            skLineSegment(sketch, "E29.3.0.26", {"start": v(-5, -45.02) * mm, "end": v(-3.03, -45.02) * mm});
            skLineSegment(sketch, "E29.3.0.27", {"start": v(-5.85, -46.23) * mm, "end": v(-5.34, -44.32) * mm});
            skLineSegment(sketch, "E29.3.1.0", {"start": v(-9.15, -26.8) * mm, "end": v(-5.85, -26.8) * mm});
            skLineSegment(sketch, "E29.3.1.1", {"start": v(-11.47, -26.1) * mm, "end": v(-13.03, -31.94) * mm});
            skLineSegment(sketch, "E29.3.1.2", {"start": v(-8.27, -21.52) * mm, "end": v(-9.36, -25.6) * mm});
            skLineSegment(sketch, "E29.3.1.3", {"start": v(-1.4, -19.5) * mm, "end": v(-3.03, -25.6) * mm});
            skLineSegment(sketch, "E29.3.1.4", {"start": v(-4.4, -21.4) * mm, "end": v(-7.7, -21.4) * mm});
            skLineSegment(sketch, "E29.3.1.5", {"start": v(-5.35, -32.2) * mm, "end": v(-12.53, -32.2) * mm});
            skLineSegment(sketch, "E29.3.1.6", {"start": v(-3.37, -19.5) * mm, "end": v(-5, -25.6) * mm});
            skLineSegment(sketch, "E29.3.1.7", {"start": v(-6.79, -30.29) * mm, "end": v(-10.1, -30.29) * mm});
            skLineSegment(sketch, "E29.3.1.8", {"start": v(-5.34, -24.9) * mm, "end": v(-8.64, -24.9) * mm});
            skLineSegment(sketch, "E29.3.1.9", {"start": v(-5.14, -26.1) * mm, "end": v(-6.23, -30.18) * mm});
            skLineSegment(sketch, "E29.3.1.10", {"start": v(-3.17, -26.1) * mm, "end": v(-4.78, -32.11) * mm});
            skLineSegment(sketch, "E29.3.1.11", {"start": v(-11.33, -25.6) * mm, "end": v(-9.76, -19.74) * mm});
            skLineSegment(sketch, "E29.3.1.12", {"start": v(-9.3, -19.5) * mm, "end": v(-3.9, -19.5) * mm});
            skLineSegment(sketch, "E29.3.1.13", {"start": v(-9.76, -19.74) * mm, "end": v(-8.27, -21.52) * mm});
            skLineSegment(sketch, "E29.3.1.14", {"start": v(-9.36, -25.6) * mm, "end": v(-11.33, -25.6) * mm});
            skLineSegment(sketch, "E29.3.1.15", {"start": v(-10.54, -30) * mm, "end": v(-9.5, -26.1) * mm});
            skLineSegment(sketch, "E29.3.1.16", {"start": v(-7.7, -21.4) * mm, "end": v(-9.3, -19.5) * mm});
            skLineSegment(sketch, "E29.3.1.17", {"start": v(-12.53, -32.2) * mm, "end": v(-10.1, -30.29) * mm});
            skLineSegment(sketch, "E29.3.1.18", {"start": v(-3.37, -19.5) * mm, "end": v(-1.4, -19.5) * mm});
            skLineSegment(sketch, "E29.3.1.19", {"start": v(-9.5, -26.1) * mm, "end": v(-11.47, -26.1) * mm});
            skLineSegment(sketch, "E29.3.1.20", {"start": v(-13.03, -31.94) * mm, "end": v(-10.54, -30) * mm});
            skLineSegment(sketch, "E29.3.1.21", {"start": v(-5.35, -32.2) * mm, "end": v(-6.79, -30.29) * mm});
            skLineSegment(sketch, "E29.3.1.22", {"start": v(-3.9, -19.5) * mm, "end": v(-4.4, -21.4) * mm});
            skLineSegment(sketch, "E29.3.1.23", {"start": v(-6.23, -30.18) * mm, "end": v(-4.78, -32.11) * mm});
            skLineSegment(sketch, "E29.3.1.24", {"start": v(-8.64, -24.9) * mm, "end": v(-9.15, -26.8) * mm});
            skLineSegment(sketch, "E29.3.1.25", {"start": v(-5.14, -26.1) * mm, "end": v(-3.17, -26.1) * mm});
            skLineSegment(sketch, "E29.3.1.26", {"start": v(-5, -25.6) * mm, "end": v(-3.03, -25.6) * mm});
            skLineSegment(sketch, "E29.3.1.27", {"start": v(-5.85, -26.8) * mm, "end": v(-5.34, -24.9) * mm});
            skLineSegment(sketch, "E29.3.2.0", {"start": v(-9.15, -7.37) * mm, "end": v(-5.85, -7.37) * mm});
            skLineSegment(sketch, "E29.3.2.1", {"start": v(-11.47, -6.67) * mm, "end": v(-13.03, -12.51) * mm});
            skLineSegment(sketch, "E29.3.2.2", {"start": v(-8.27, -2.1) * mm, "end": v(-9.36, -6.16) * mm});
            skLineSegment(sketch, "E29.3.2.3", {"start": v(-1.4, -0.06) * mm, "end": v(-3.03, -6.16) * mm});
            skLineSegment(sketch, "E29.3.2.4", {"start": v(-4.4, -1.97) * mm, "end": v(-7.7, -1.97) * mm});
            skLineSegment(sketch, "E29.3.2.5", {"start": v(-5.35, -12.76) * mm, "end": v(-12.53, -12.76) * mm});
            skLineSegment(sketch, "E29.3.2.6", {"start": v(-3.37, -0.06) * mm, "end": v(-5, -6.16) * mm});
            skLineSegment(sketch, "E29.3.2.7", {"start": v(-6.79, -10.86) * mm, "end": v(-10.1, -10.86) * mm});
            skLineSegment(sketch, "E29.3.2.8", {"start": v(-5.34, -5.46) * mm, "end": v(-8.64, -5.46) * mm});
            skLineSegment(sketch, "E29.3.2.9", {"start": v(-5.14, -6.67) * mm, "end": v(-6.23, -10.75) * mm});
            skLineSegment(sketch, "E29.3.2.10", {"start": v(-3.17, -6.67) * mm, "end": v(-4.78, -12.68) * mm});
            skLineSegment(sketch, "E29.3.2.11", {"start": v(-11.33, -6.16) * mm, "end": v(-9.76, -0.31) * mm});
            skLineSegment(sketch, "E29.3.2.12", {"start": v(-9.3, -0.06) * mm, "end": v(-3.9, -0.06) * mm});
            skLineSegment(sketch, "E29.3.2.13", {"start": v(-9.76, -0.31) * mm, "end": v(-8.27, -2.1) * mm});
            skLineSegment(sketch, "E29.3.2.14", {"start": v(-9.36, -6.16) * mm, "end": v(-11.33, -6.16) * mm});
            skLineSegment(sketch, "E29.3.2.15", {"start": v(-10.54, -10.56) * mm, "end": v(-9.5, -6.67) * mm});
            skLineSegment(sketch, "E29.3.2.16", {"start": v(-7.7, -1.97) * mm, "end": v(-9.3, -0.06) * mm});
            skLineSegment(sketch, "E29.3.2.17", {"start": v(-12.53, -12.76) * mm, "end": v(-10.1, -10.86) * mm});
            skLineSegment(sketch, "E29.3.2.18", {"start": v(-3.37, -0.06) * mm, "end": v(-1.4, -0.06) * mm});
            skLineSegment(sketch, "E29.3.2.19", {"start": v(-9.5, -6.67) * mm, "end": v(-11.47, -6.67) * mm});
            skLineSegment(sketch, "E29.3.2.20", {"start": v(-13.03, -12.51) * mm, "end": v(-10.54, -10.56) * mm});
            skLineSegment(sketch, "E29.3.2.21", {"start": v(-5.35, -12.76) * mm, "end": v(-6.79, -10.86) * mm});
            skLineSegment(sketch, "E29.3.2.22", {"start": v(-3.9, -0.06) * mm, "end": v(-4.4, -1.97) * mm});
            skLineSegment(sketch, "E29.3.2.23", {"start": v(-6.23, -10.75) * mm, "end": v(-4.78, -12.68) * mm});
            skLineSegment(sketch, "E29.3.2.24", {"start": v(-8.64, -5.46) * mm, "end": v(-9.15, -7.37) * mm});
            skLineSegment(sketch, "E29.3.2.25", {"start": v(-5.14, -6.67) * mm, "end": v(-3.17, -6.67) * mm});
            skLineSegment(sketch, "E29.3.2.26", {"start": v(-5, -6.16) * mm, "end": v(-3.03, -6.16) * mm});
            skLineSegment(sketch, "E29.3.2.27", {"start": v(-5.85, -7.37) * mm, "end": v(-5.34, -5.46) * mm});
            skLineSegment(sketch, "E29.4.0.0", {"start": v(-19.3, -46.23) * mm, "end": v(-16, -46.23) * mm});
            skLineSegment(sketch, "E29.4.0.1", {"start": v(-21.6, -45.53) * mm, "end": v(-23.17, -51.37) * mm});
            skLineSegment(sketch, "E29.4.0.2", {"start": v(-18.4, -40.95) * mm, "end": v(-19.5, -45.02) * mm});
            skLineSegment(sketch, "E29.4.0.3", {"start": v(-11.54, -38.93) * mm, "end": v(-13.17, -45.02) * mm});
            skLineSegment(sketch, "E29.4.0.4", {"start": v(-14.55, -40.83) * mm, "end": v(-17.85, -40.83) * mm});
            skLineSegment(sketch, "E29.4.0.5", {"start": v(-15.5, -51.63) * mm, "end": v(-22.67, -51.63) * mm});
            skLineSegment(sketch, "E29.4.0.6", {"start": v(-13.5, -38.93) * mm, "end": v(-15.14, -45.02) * mm});
            skLineSegment(sketch, "E29.4.0.7", {"start": v(-16.93, -49.72) * mm, "end": v(-20.23, -49.72) * mm});
            skLineSegment(sketch, "E29.4.0.8", {"start": v(-15.48, -44.32) * mm, "end": v(-18.78, -44.32) * mm});
            skLineSegment(sketch, "E29.4.0.9", {"start": v(-15.28, -45.53) * mm, "end": v(-16.37, -49.61) * mm});
            skLineSegment(sketch, "E29.4.0.10", {"start": v(-13.3, -45.53) * mm, "end": v(-14.92, -51.54) * mm});
            skLineSegment(sketch, "E29.4.0.11", {"start": v(-21.47, -45.02) * mm, "end": v(-19.9, -39.17) * mm});
            skLineSegment(sketch, "E29.4.0.12", {"start": v(-19.45, -38.93) * mm, "end": v(-14.04, -38.93) * mm});
            skLineSegment(sketch, "E29.4.0.13", {"start": v(-19.9, -39.17) * mm, "end": v(-18.4, -40.95) * mm});
            skLineSegment(sketch, "E29.4.0.14", {"start": v(-19.5, -45.02) * mm, "end": v(-21.47, -45.02) * mm});
            skLineSegment(sketch, "E29.4.0.15", {"start": v(-20.68, -49.42) * mm, "end": v(-19.63, -45.53) * mm});
            skLineSegment(sketch, "E29.4.0.16", {"start": v(-17.85, -40.83) * mm, "end": v(-19.45, -38.93) * mm});
            skLineSegment(sketch, "E29.4.0.17", {"start": v(-22.67, -51.63) * mm, "end": v(-20.23, -49.72) * mm});
            skLineSegment(sketch, "E29.4.0.18", {"start": v(-13.5, -38.93) * mm, "end": v(-11.54, -38.93) * mm});
            skLineSegment(sketch, "E29.4.0.19", {"start": v(-19.63, -45.53) * mm, "end": v(-21.6, -45.53) * mm});
            skLineSegment(sketch, "E29.4.0.20", {"start": v(-23.17, -51.37) * mm, "end": v(-20.68, -49.42) * mm});
            skLineSegment(sketch, "E29.4.0.21", {"start": v(-15.5, -51.63) * mm, "end": v(-16.93, -49.72) * mm});
            skLineSegment(sketch, "E29.4.0.22", {"start": v(-14.04, -38.93) * mm, "end": v(-14.55, -40.83) * mm});
            skLineSegment(sketch, "E29.4.0.23", {"start": v(-16.37, -49.61) * mm, "end": v(-14.92, -51.54) * mm});
            skLineSegment(sketch, "E29.4.0.24", {"start": v(-18.78, -44.32) * mm, "end": v(-19.04, -45.28) * mm});
            skLineSegment(sketch, "E29.4.0.25", {"start": v(-15.28, -45.53) * mm, "end": v(-13.3, -45.53) * mm});
            skLineSegment(sketch, "E29.4.0.26", {"start": v(-15.14, -45.02) * mm, "end": v(-13.17, -45.02) * mm});
            skLineSegment(sketch, "E29.4.0.27", {"start": v(-16, -46.23) * mm, "end": v(-15.48, -44.32) * mm});
            skLineSegment(sketch, "E29.4.1.0", {"start": v(-19.3, -26.8) * mm, "end": v(-16, -26.8) * mm});
            skLineSegment(sketch, "E29.4.1.1", {"start": v(-21.6, -26.1) * mm, "end": v(-23.17, -31.94) * mm});
            skLineSegment(sketch, "E29.4.1.2", {"start": v(-18.4, -21.52) * mm, "end": v(-19.5, -25.6) * mm});
            skLineSegment(sketch, "E29.4.1.3", {"start": v(-11.54, -19.5) * mm, "end": v(-13.17, -25.6) * mm});
            skLineSegment(sketch, "E29.4.1.4", {"start": v(-14.55, -21.4) * mm, "end": v(-17.85, -21.4) * mm});
            skLineSegment(sketch, "E29.4.1.5", {"start": v(-15.5, -32.2) * mm, "end": v(-22.67, -32.2) * mm});
            skLineSegment(sketch, "E29.4.1.6", {"start": v(-13.5, -19.5) * mm, "end": v(-15.14, -25.6) * mm});
            skLineSegment(sketch, "E29.4.1.7", {"start": v(-16.93, -30.29) * mm, "end": v(-20.23, -30.29) * mm});
            skLineSegment(sketch, "E29.4.1.8", {"start": v(-15.48, -24.9) * mm, "end": v(-18.78, -24.9) * mm});
            skLineSegment(sketch, "E29.4.1.9", {"start": v(-15.28, -26.1) * mm, "end": v(-16.37, -30.18) * mm});
            skLineSegment(sketch, "E29.4.1.10", {"start": v(-13.3, -26.1) * mm, "end": v(-14.92, -32.11) * mm});
            skLineSegment(sketch, "E29.4.1.11", {"start": v(-21.47, -25.6) * mm, "end": v(-19.9, -19.74) * mm});
            skLineSegment(sketch, "E29.4.1.12", {"start": v(-19.45, -19.5) * mm, "end": v(-14.04, -19.5) * mm});
            skLineSegment(sketch, "E29.4.1.13", {"start": v(-19.9, -19.74) * mm, "end": v(-18.4, -21.52) * mm});
            skLineSegment(sketch, "E29.4.1.14", {"start": v(-19.5, -25.6) * mm, "end": v(-21.47, -25.6) * mm});
            skLineSegment(sketch, "E29.4.1.15", {"start": v(-20.68, -30) * mm, "end": v(-19.63, -26.1) * mm});
            skLineSegment(sketch, "E29.4.1.16", {"start": v(-17.85, -21.4) * mm, "end": v(-19.45, -19.5) * mm});
            skLineSegment(sketch, "E29.4.1.17", {"start": v(-22.67, -32.2) * mm, "end": v(-20.23, -30.29) * mm});
            skLineSegment(sketch, "E29.4.1.18", {"start": v(-13.5, -19.5) * mm, "end": v(-11.54, -19.5) * mm});
            skLineSegment(sketch, "E29.4.1.19", {"start": v(-19.63, -26.1) * mm, "end": v(-21.6, -26.1) * mm});
            skLineSegment(sketch, "E29.4.1.20", {"start": v(-23.17, -31.94) * mm, "end": v(-20.68, -30) * mm});
            skLineSegment(sketch, "E29.4.1.21", {"start": v(-15.5, -32.2) * mm, "end": v(-16.93, -30.29) * mm});
            skLineSegment(sketch, "E29.4.1.22", {"start": v(-14.04, -19.5) * mm, "end": v(-14.55, -21.4) * mm});
            skLineSegment(sketch, "E29.4.1.23", {"start": v(-16.37, -30.18) * mm, "end": v(-14.92, -32.11) * mm});
            skLineSegment(sketch, "E29.4.1.24", {"start": v(-18.78, -24.9) * mm, "end": v(-19.3, -26.8) * mm});
            skLineSegment(sketch, "E29.4.1.25", {"start": v(-15.28, -26.1) * mm, "end": v(-13.3, -26.1) * mm});
            skLineSegment(sketch, "E29.4.1.26", {"start": v(-15.14, -25.6) * mm, "end": v(-13.17, -25.6) * mm});
            skLineSegment(sketch, "E29.4.1.27", {"start": v(-16, -26.8) * mm, "end": v(-15.48, -24.9) * mm});
            skLineSegment(sketch, "E29.4.2.0", {"start": v(-19.3, -7.37) * mm, "end": v(-16, -7.37) * mm});
            skLineSegment(sketch, "E29.4.2.1", {"start": v(-21.6, -6.67) * mm, "end": v(-23.17, -12.51) * mm});
            skLineSegment(sketch, "E29.4.2.2", {"start": v(-18.4, -2.1) * mm, "end": v(-19.5, -6.16) * mm});
            skLineSegment(sketch, "E29.4.2.3", {"start": v(-11.54, -0.06) * mm, "end": v(-13.17, -6.16) * mm});
            skLineSegment(sketch, "E29.4.2.4", {"start": v(-14.55, -1.97) * mm, "end": v(-17.85, -1.97) * mm});
            skLineSegment(sketch, "E29.4.2.5", {"start": v(-15.5, -12.76) * mm, "end": v(-22.67, -12.76) * mm});
            skLineSegment(sketch, "E29.4.2.6", {"start": v(-13.5, -0.06) * mm, "end": v(-15.14, -6.16) * mm});
            skLineSegment(sketch, "E29.4.2.7", {"start": v(-16.93, -10.86) * mm, "end": v(-20.23, -10.86) * mm});
            skLineSegment(sketch, "E29.4.2.8", {"start": v(-15.48, -5.46) * mm, "end": v(-18.78, -5.46) * mm});
            skLineSegment(sketch, "E29.4.2.9", {"start": v(-15.28, -6.67) * mm, "end": v(-16.37, -10.75) * mm});
            skLineSegment(sketch, "E29.4.2.10", {"start": v(-13.3, -6.67) * mm, "end": v(-14.92, -12.68) * mm});
            skLineSegment(sketch, "E29.4.2.11", {"start": v(-21.47, -6.16) * mm, "end": v(-19.9, -0.31) * mm});
            skLineSegment(sketch, "E29.4.2.12", {"start": v(-19.45, -0.06) * mm, "end": v(-14.04, -0.06) * mm});
            skLineSegment(sketch, "E29.4.2.13", {"start": v(-19.9, -0.31) * mm, "end": v(-18.4, -2.1) * mm});
            skLineSegment(sketch, "E29.4.2.14", {"start": v(-19.5, -6.16) * mm, "end": v(-21.47, -6.16) * mm});
            skLineSegment(sketch, "E29.4.2.15", {"start": v(-20.68, -10.56) * mm, "end": v(-19.63, -6.67) * mm});
            skLineSegment(sketch, "E29.4.2.16", {"start": v(-17.85, -1.97) * mm, "end": v(-19.45, -0.06) * mm});
            skLineSegment(sketch, "E29.4.2.17", {"start": v(-22.67, -12.76) * mm, "end": v(-20.23, -10.86) * mm});
            skLineSegment(sketch, "E29.4.2.18", {"start": v(-13.5, -0.06) * mm, "end": v(-11.54, -0.06) * mm});
            skLineSegment(sketch, "E29.4.2.19", {"start": v(-19.63, -6.67) * mm, "end": v(-21.6, -6.67) * mm});
            skLineSegment(sketch, "E29.4.2.20", {"start": v(-23.17, -12.51) * mm, "end": v(-20.68, -10.56) * mm});
            skLineSegment(sketch, "E29.4.2.21", {"start": v(-15.5, -12.76) * mm, "end": v(-16.93, -10.86) * mm});
            skLineSegment(sketch, "E29.4.2.22", {"start": v(-14.04, -0.06) * mm, "end": v(-14.55, -1.97) * mm});
            skLineSegment(sketch, "E29.4.2.23", {"start": v(-16.37, -10.75) * mm, "end": v(-14.92, -12.68) * mm});
            skLineSegment(sketch, "E29.4.2.24", {"start": v(-18.78, -5.46) * mm, "end": v(-19.3, -7.37) * mm});
            skLineSegment(sketch, "E29.4.2.25", {"start": v(-15.28, -6.67) * mm, "end": v(-13.3, -6.67) * mm});
            skLineSegment(sketch, "E29.4.2.26", {"start": v(-15.14, -6.16) * mm, "end": v(-13.17, -6.16) * mm});
            skLineSegment(sketch, "E29.4.2.27", {"start": v(-16, -7.37) * mm, "end": v(-15.48, -5.46) * mm});
            skLineSegment(sketch, "E29.direction1", {"start": v(17.39, -51.37) * mm, "end": v(7.25, -51.37) * mm, "construction": true});
            skLineSegment(sketch, "E29.direction2", {"start": v(17.39, -51.37) * mm, "end": v(17.39, -31.94) * mm, "construction": true});
            skLineSegment(sketch, "E30.direction1", {"start": v(7.75, -12.76) * mm, "end": v(33.15, -12.76) * mm, "construction": true});
            skLineSegment(sketch, "E30.direction2", {"start": v(7.75, -12.76) * mm, "end": v(7.75, 6.29) * mm, "construction": true});
            skLineSegment(sketch, "E31.0.0.1", {"start": v(26.01, 17.08) * mm, "end": v(22.7, 17.08) * mm});
            skLineSegment(sketch, "E31.3.0.1", {"start": v(21.26, 11.68) * mm, "end": v(24.56, 11.68) * mm});
            skLineSegment(sketch, "E31.6.0.1", {"start": v(15.87, 17.08) * mm, "end": v(12.57, 17.08) * mm});
            skLineSegment(sketch, "E31.9.0.1", {"start": v(10.97, 18.99) * mm, "end": v(16.38, 18.99) * mm});
            skLineSegment(sketch, "E31.12.0.1", {"start": v(25.08, 13.59) * mm, "end": v(21.77, 13.59) * mm});
            skLineSegment(sketch, "E31.15.0.1", {"start": v(27.05, 18.99) * mm, "end": v(25.41, 12.9) * mm});
            skLineSegment(sketch, "E31.18.0.1", {"start": v(17.39, 6.54) * mm, "end": v(19.88, 8.49) * mm});
            skLineSegment(sketch, "E31.21.0.1", {"start": v(22.15, 16.96) * mm, "end": v(21.06, 12.9) * mm});
            skLineSegment(sketch, "E31.24.0.1", {"start": v(25.28, 12.38) * mm, "end": v(27.25, 12.38) * mm});
            skLineSegment(sketch, "E31.27.0.1", {"start": v(24.18, 8.3) * mm, "end": v(25.64, 6.37) * mm});
            skLineSegment(sketch, "E31.30.0.1", {"start": v(17.89, 6.29) * mm, "end": v(20.33, 8.2) * mm});
            skLineSegment(sketch, "E31.33.0.1", {"start": v(17.11, 12.38) * mm, "end": v(15.5, 6.37) * mm});
            skLineSegment(sketch, "E31.36.0.1", {"start": v(12.57, 17.08) * mm, "end": v(10.97, 18.99) * mm});
            skLineSegment(sketch, "E31.39.0.1", {"start": v(27.05, 18.99) * mm, "end": v(29.02, 18.99) * mm});
            skLineSegment(sketch, "E31.42.0.1", {"start": v(19.88, 8.49) * mm, "end": v(20.92, 12.38) * mm});
            skLineSegment(sketch, "E31.45.0.1", {"start": v(29.02, 18.99) * mm, "end": v(27.39, 12.9) * mm});
            skLineSegment(sketch, "E31.48.0.1", {"start": v(23.63, 8.2) * mm, "end": v(20.33, 8.2) * mm});
            skLineSegment(sketch, "E31.51.0.1", {"start": v(16.9, 18.99) * mm, "end": v(15.27, 12.9) * mm});
            skLineSegment(sketch, "E31.54.0.1", {"start": v(25.41, 12.9) * mm, "end": v(27.39, 12.9) * mm});
            skLineSegment(sketch, "E31.57.0.1", {"start": v(25.06, 6.29) * mm, "end": v(17.89, 6.29) * mm});
            skLineSegment(sketch, "E31.60.0.1", {"start": v(9.74, 8.49) * mm, "end": v(10.78, 12.38) * mm});
            skLineSegment(sketch, "E31.63.0.1", {"start": v(8.95, 12.9) * mm, "end": v(10.52, 18.74) * mm});
            skLineSegment(sketch, "E31.66.0.1", {"start": v(21.11, 18.99) * mm, "end": v(26.52, 18.99) * mm});
            skLineSegment(sketch, "E31.69.0.1", {"start": v(27.25, 12.38) * mm, "end": v(25.64, 6.37) * mm});
            skLineSegment(sketch, "E31.72.0.1", {"start": v(25.28, 12.38) * mm, "end": v(24.18, 8.3) * mm});
            skLineSegment(sketch, "E31.75.0.1", {"start": v(13.49, 8.2) * mm, "end": v(10.19, 8.2) * mm});
            skLineSegment(sketch, "E31.78.0.1", {"start": v(14.04, 8.3) * mm, "end": v(15.5, 6.37) * mm});
            skLineSegment(sketch, "E31.81.0.1", {"start": v(25.06, 6.29) * mm, "end": v(23.63, 8.2) * mm});
            skLineSegment(sketch, "E31.84.0.1", {"start": v(12.01, 16.96) * mm, "end": v(10.92, 12.9) * mm});
            skLineSegment(sketch, "E31.87.0.1", {"start": v(18.95, 12.38) * mm, "end": v(17.39, 6.54) * mm});
            skLineSegment(sketch, "E31.90.0.1", {"start": v(11.12, 11.68) * mm, "end": v(14.43, 11.68) * mm});
            skLineSegment(sketch, "E31.93.0.1", {"start": v(14.93, 6.29) * mm, "end": v(13.49, 8.2) * mm});
            skLineSegment(sketch, "E31.96.0.1", {"start": v(14.93, 6.29) * mm, "end": v(7.75, 6.29) * mm});
            skLineSegment(sketch, "E31.99.0.1", {"start": v(15.14, 12.38) * mm, "end": v(14.04, 8.3) * mm});
            skLineSegment(sketch, "E31.102.0.1", {"start": v(19.09, 12.9) * mm, "end": v(20.65, 18.74) * mm});
            skLineSegment(sketch, "E31.105.0.1", {"start": v(14.94, 13.59) * mm, "end": v(11.63, 13.59) * mm});
            skLineSegment(sketch, "E31.108.0.1", {"start": v(20.65, 18.74) * mm, "end": v(22.15, 16.96) * mm});
            skLineSegment(sketch, "E31.111.0.1", {"start": v(18.88, 18.99) * mm, "end": v(17.25, 12.9) * mm});
            skLineSegment(sketch, "E31.114.0.1", {"start": v(10.52, 18.74) * mm, "end": v(12.01, 16.96) * mm});
            skLineSegment(sketch, "E31.117.0.1", {"start": v(10.92, 12.9) * mm, "end": v(8.95, 12.9) * mm});
            skLineSegment(sketch, "E31.120.0.1", {"start": v(7.75, 6.29) * mm, "end": v(10.19, 8.2) * mm});
            skLineSegment(sketch, "E31.123.0.1", {"start": v(15.14, 12.38) * mm, "end": v(17.11, 12.38) * mm});
            skLineSegment(sketch, "E31.126.0.1", {"start": v(11.63, 13.59) * mm, "end": v(11.12, 11.68) * mm});
            skLineSegment(sketch, "E31.129.0.1", {"start": v(16.38, 18.99) * mm, "end": v(15.87, 17.08) * mm});
            skLineSegment(sketch, "E31.132.0.1", {"start": v(21.77, 13.59) * mm, "end": v(21.26, 11.68) * mm});
            skLineSegment(sketch, "E31.135.0.1", {"start": v(14.43, 11.68) * mm, "end": v(14.94, 13.59) * mm});
            skLineSegment(sketch, "E31.138.0.1", {"start": v(21.06, 12.9) * mm, "end": v(19.09, 12.9) * mm});
            skLineSegment(sketch, "E31.141.0.1", {"start": v(26.52, 18.99) * mm, "end": v(26.01, 17.08) * mm});
            skLineSegment(sketch, "E31.144.0.1", {"start": v(15.27, 12.9) * mm, "end": v(17.25, 12.9) * mm});
            skLineSegment(sketch, "E31.147.0.1", {"start": v(20.92, 12.38) * mm, "end": v(18.95, 12.38) * mm});
            skLineSegment(sketch, "E31.150.0.1", {"start": v(16.9, 18.99) * mm, "end": v(18.88, 18.99) * mm});
            skLineSegment(sketch, "E31.153.0.1", {"start": v(24.56, 11.68) * mm, "end": v(25.08, 13.59) * mm});
            skLineSegment(sketch, "E31.156.0.1", {"start": v(22.7, 17.08) * mm, "end": v(21.11, 18.99) * mm});
            skLineSegment(sketch, "E31.159.0.1", {"start": v(10.78, 12.38) * mm, "end": v(8.81, 12.38) * mm});
            skLineSegment(sketch, "E31.162.0.1", {"start": v(7.25, 6.54) * mm, "end": v(9.74, 8.49) * mm});
            skLineSegment(sketch, "E31.165.0.1", {"start": v(8.81, 12.38) * mm, "end": v(7.25, 6.54) * mm});
            skLineSegment(sketch, "E32.0.1.0", {"start": v(27.05, 43.12) * mm, "end": v(25.41, 37.02) * mm});
            skLineSegment(sketch, "E32.0.1.1", {"start": v(25.08, 37.72) * mm, "end": v(21.77, 37.72) * mm});
            skLineSegment(sketch, "E32.0.1.2", {"start": v(26.01, 41.21) * mm, "end": v(22.7, 41.21) * mm});
            skLineSegment(sketch, "E32.0.1.3", {"start": v(22.15, 41.09) * mm, "end": v(21.06, 37.02) * mm});
            skLineSegment(sketch, "E32.0.1.4", {"start": v(8.81, 36.51) * mm, "end": v(7.25, 30.67) * mm});
            skLineSegment(sketch, "E32.0.1.5", {"start": v(18.95, 36.51) * mm, "end": v(17.39, 30.67) * mm});
            skLineSegment(sketch, "E32.0.1.6", {"start": v(8.95, 37.02) * mm, "end": v(10.52, 42.87) * mm});
            skLineSegment(sketch, "E32.0.1.7", {"start": v(25.28, 36.51) * mm, "end": v(24.18, 32.43) * mm});
            skLineSegment(sketch, "E32.0.1.8", {"start": v(17.11, 36.51) * mm, "end": v(15.5, 30.5) * mm});
            skLineSegment(sketch, "E32.0.1.9", {"start": v(27.25, 36.51) * mm, "end": v(25.64, 30.5) * mm});
            skLineSegment(sketch, "E32.0.1.10", {"start": v(15.14, 36.51) * mm, "end": v(14.04, 32.43) * mm});
            skLineSegment(sketch, "E32.0.1.11", {"start": v(18.88, 43.12) * mm, "end": v(17.25, 37.02) * mm});
            skLineSegment(sketch, "E32.0.1.12", {"start": v(12.01, 41.09) * mm, "end": v(10.92, 37.02) * mm});
            skLineSegment(sketch, "E32.0.1.13", {"start": v(13.49, 32.32) * mm, "end": v(10.19, 32.32) * mm});
            skLineSegment(sketch, "E32.0.1.14", {"start": v(21.11, 43.12) * mm, "end": v(26.52, 43.12) * mm});
            skLineSegment(sketch, "E32.0.1.15", {"start": v(21.26, 35.81) * mm, "end": v(24.56, 35.81) * mm});
            skLineSegment(sketch, "E32.0.1.16", {"start": v(19.09, 37.02) * mm, "end": v(20.65, 42.87) * mm});
            skLineSegment(sketch, "E32.0.1.17", {"start": v(29.02, 43.12) * mm, "end": v(27.39, 37.02) * mm});
            skLineSegment(sketch, "E32.0.1.18", {"start": v(10.97, 43.12) * mm, "end": v(16.38, 43.12) * mm});
            skLineSegment(sketch, "E32.0.1.19", {"start": v(25.06, 30.42) * mm, "end": v(17.89, 30.42) * mm});
            skLineSegment(sketch, "E32.0.1.20", {"start": v(14.93, 30.42) * mm, "end": v(7.75, 30.42) * mm});
            skLineSegment(sketch, "E32.0.1.21", {"start": v(23.63, 32.32) * mm, "end": v(20.33, 32.32) * mm});
            skLineSegment(sketch, "E32.0.1.22", {"start": v(16.9, 43.12) * mm, "end": v(15.27, 37.02) * mm});
            skLineSegment(sketch, "E32.0.1.23", {"start": v(22.7, 41.21) * mm, "end": v(21.11, 43.12) * mm});
            skLineSegment(sketch, "E32.0.1.24", {"start": v(21.06, 37.02) * mm, "end": v(19.09, 37.02) * mm});
            skLineSegment(sketch, "E32.0.1.25", {"start": v(7.25, 30.67) * mm, "end": v(9.74, 32.62) * mm});
            skLineSegment(sketch, "E32.0.1.26", {"start": v(17.89, 30.42) * mm, "end": v(20.33, 32.32) * mm});
            skLineSegment(sketch, "E32.0.1.27", {"start": v(25.41, 37.02) * mm, "end": v(27.39, 37.02) * mm});
            skLineSegment(sketch, "E32.0.1.28", {"start": v(26.52, 43.12) * mm, "end": v(26.01, 41.21) * mm});
            skLineSegment(sketch, "E32.0.1.29", {"start": v(10.52, 42.87) * mm, "end": v(12.01, 41.09) * mm});
            skLineSegment(sketch, "E32.0.1.30", {"start": v(9.74, 32.62) * mm, "end": v(10.78, 36.51) * mm});
            skLineSegment(sketch, "E32.0.1.31", {"start": v(16.9, 43.12) * mm, "end": v(18.88, 43.12) * mm});
            skLineSegment(sketch, "E32.0.1.32", {"start": v(20.65, 42.87) * mm, "end": v(22.15, 41.09) * mm});
            skLineSegment(sketch, "E32.0.1.33", {"start": v(7.75, 30.42) * mm, "end": v(10.19, 32.32) * mm});
            skLineSegment(sketch, "E32.0.1.34", {"start": v(10.92, 37.02) * mm, "end": v(8.95, 37.02) * mm});
            skLineSegment(sketch, "E32.0.1.35", {"start": v(15.87, 41.21) * mm, "end": v(12.57, 41.21) * mm});
            skLineSegment(sketch, "E32.0.1.36", {"start": v(12.57, 41.21) * mm, "end": v(10.97, 43.12) * mm});
            skLineSegment(sketch, "E32.0.1.37", {"start": v(15.27, 37.02) * mm, "end": v(17.25, 37.02) * mm});
            skLineSegment(sketch, "E32.0.1.38", {"start": v(14.04, 32.43) * mm, "end": v(15.5, 30.5) * mm});
            skLineSegment(sketch, "E32.0.1.39", {"start": v(25.06, 30.42) * mm, "end": v(23.63, 32.32) * mm});
            skLineSegment(sketch, "E32.0.1.40", {"start": v(11.12, 35.81) * mm, "end": v(14.43, 35.81) * mm});
            skLineSegment(sketch, "E32.0.1.41", {"start": v(25.28, 36.51) * mm, "end": v(27.25, 36.51) * mm});
            skLineSegment(sketch, "E32.0.1.42", {"start": v(10.78, 36.51) * mm, "end": v(8.81, 36.51) * mm});
            skLineSegment(sketch, "E32.0.1.43", {"start": v(16.38, 43.12) * mm, "end": v(15.87, 41.21) * mm});
            skLineSegment(sketch, "E32.0.1.44", {"start": v(15.14, 36.51) * mm, "end": v(17.11, 36.51) * mm});
            skLineSegment(sketch, "E32.0.1.45", {"start": v(14.93, 30.42) * mm, "end": v(13.49, 32.32) * mm});
            skLineSegment(sketch, "E32.0.1.46", {"start": v(24.18, 32.43) * mm, "end": v(25.64, 30.5) * mm});
            skLineSegment(sketch, "E32.0.1.47", {"start": v(27.05, 43.12) * mm, "end": v(29.02, 43.12) * mm});
            skLineSegment(sketch, "E32.0.1.48", {"start": v(17.39, 30.67) * mm, "end": v(19.88, 32.62) * mm});
            skLineSegment(sketch, "E32.0.1.49", {"start": v(19.88, 32.62) * mm, "end": v(20.92, 36.51) * mm});
            skLineSegment(sketch, "E32.0.1.50", {"start": v(20.92, 36.51) * mm, "end": v(18.95, 36.51) * mm});
            skLineSegment(sketch, "E32.0.1.51", {"start": v(14.94, 37.72) * mm, "end": v(11.63, 37.72) * mm});
            skLineSegment(sketch, "E32.0.1.52", {"start": v(24.56, 35.81) * mm, "end": v(25.08, 37.72) * mm});
            skLineSegment(sketch, "E32.0.1.53", {"start": v(21.77, 37.72) * mm, "end": v(21.26, 35.81) * mm});
            skLineSegment(sketch, "E32.0.1.54", {"start": v(11.63, 37.72) * mm, "end": v(11.12, 35.81) * mm});
            skLineSegment(sketch, "E32.0.1.55", {"start": v(14.43, 35.81) * mm, "end": v(14.94, 37.72) * mm});
            skLineSegment(sketch, "E32.direction1", {"start": v(7.25, 6.54) * mm, "end": v(32.65, 6.54) * mm, "construction": true});
            skLineSegment(sketch, "E32.direction2", {"start": v(7.25, 6.54) * mm, "end": v(7.25, 30.67) * mm, "construction": true});
            skLineSegment(sketch, "E33.1.0.0", {"start": v(-8.82, 12.38) * mm, "end": v(-10.43, 6.37) * mm});
            skLineSegment(sketch, "E33.1.0.1", {"start": v(-17.19, 18.99) * mm, "end": v(-18.82, 12.9) * mm});
            skLineSegment(sketch, "E33.1.0.2", {"start": v(-17.12, 12.38) * mm, "end": v(-18.68, 6.54) * mm});
            skLineSegment(sketch, "E33.1.0.3", {"start": v(-27.26, 12.38) * mm, "end": v(-28.82, 6.54) * mm});
            skLineSegment(sketch, "E33.1.0.4", {"start": v(-25.1, 18.99) * mm, "end": v(-19.69, 18.99) * mm});
            skLineSegment(sketch, "E33.1.0.5", {"start": v(-14.96, 18.99) * mm, "end": v(-9.55, 18.99) * mm});
            skLineSegment(sketch, "E33.1.0.6", {"start": v(-16.98, 12.9) * mm, "end": v(-15.41, 18.74) * mm});
            skLineSegment(sketch, "E33.1.0.7", {"start": v(-27.12, 12.9) * mm, "end": v(-25.55, 18.74) * mm});
            skLineSegment(sketch, "E33.1.0.8", {"start": v(-21.14, 6.29) * mm, "end": v(-28.32, 6.29) * mm});
            skLineSegment(sketch, "E33.1.0.9", {"start": v(-11, 6.29) * mm, "end": v(-18.18, 6.29) * mm});
            skLineSegment(sketch, "E33.1.0.10", {"start": v(-7.05, 18.99) * mm, "end": v(-8.68, 12.9) * mm});
            skLineSegment(sketch, "E33.1.0.11", {"start": v(-18.96, 12.38) * mm, "end": v(-20.57, 6.37) * mm});
            skLineSegment(sketch, "E33.1.0.12", {"start": v(-9.02, 18.99) * mm, "end": v(-10.65, 12.9) * mm});
            skLineSegment(sketch, "E33.1.0.13", {"start": v(-14.8, 11.68) * mm, "end": v(-11.5, 11.68) * mm});
            skLineSegment(sketch, "E33.1.0.14", {"start": v(-20.2, 17.08) * mm, "end": v(-23.5, 17.08) * mm});
            skLineSegment(sketch, "E33.1.0.15", {"start": v(-24.94, 11.68) * mm, "end": v(-21.64, 11.68) * mm});
            skLineSegment(sketch, "E33.1.0.16", {"start": v(-12.44, 8.2) * mm, "end": v(-15.74, 8.2) * mm});
            skLineSegment(sketch, "E33.1.0.17", {"start": v(-13.92, 16.96) * mm, "end": v(-15, 12.9) * mm});
            skLineSegment(sketch, "E33.1.0.18", {"start": v(-16.19, 8.49) * mm, "end": v(-15.14, 12.38) * mm});
            skLineSegment(sketch, "E33.1.0.19", {"start": v(-19.16, 18.99) * mm, "end": v(-20.8, 12.9) * mm});
            skLineSegment(sketch, "E33.1.0.20", {"start": v(-25.28, 12.38) * mm, "end": v(-27.26, 12.38) * mm});
            skLineSegment(sketch, "E33.1.0.21", {"start": v(-25.55, 18.74) * mm, "end": v(-24.06, 16.96) * mm});
            skLineSegment(sketch, "E33.1.0.22", {"start": v(-28.82, 6.54) * mm, "end": v(-26.33, 8.49) * mm});
            skLineSegment(sketch, "E33.1.0.23", {"start": v(-10.65, 12.9) * mm, "end": v(-8.68, 12.9) * mm});
            skLineSegment(sketch, "E33.1.0.24", {"start": v(-10.06, 17.08) * mm, "end": v(-13.36, 17.08) * mm});
            skLineSegment(sketch, "E33.1.0.25", {"start": v(-18.18, 6.29) * mm, "end": v(-15.74, 8.2) * mm});
            skLineSegment(sketch, "E33.1.0.26", {"start": v(-20.93, 12.38) * mm, "end": v(-22.02, 8.3) * mm});
            skLineSegment(sketch, "E33.1.0.27", {"start": v(-10.8, 12.38) * mm, "end": v(-8.82, 12.38) * mm});
            skLineSegment(sketch, "E33.1.0.28", {"start": v(-10.8, 12.38) * mm, "end": v(-11.88, 8.3) * mm});
            skLineSegment(sketch, "E33.1.0.29", {"start": v(-9.02, 18.99) * mm, "end": v(-7.05, 18.99) * mm});
            skLineSegment(sketch, "E33.1.0.30", {"start": v(-9.55, 18.99) * mm, "end": v(-10.06, 17.08) * mm});
            skLineSegment(sketch, "E33.1.0.31", {"start": v(-24.06, 16.96) * mm, "end": v(-25.15, 12.9) * mm});
            skLineSegment(sketch, "E33.1.0.32", {"start": v(-20.8, 12.9) * mm, "end": v(-18.82, 12.9) * mm});
            skLineSegment(sketch, "E33.1.0.33", {"start": v(-11.88, 8.3) * mm, "end": v(-10.43, 6.37) * mm});
            skLineSegment(sketch, "E33.1.0.34", {"start": v(-28.32, 6.29) * mm, "end": v(-25.88, 8.2) * mm});
            skLineSegment(sketch, "E33.1.0.35", {"start": v(-22.02, 8.3) * mm, "end": v(-20.57, 6.37) * mm});
            skLineSegment(sketch, "E33.1.0.36", {"start": v(-21.14, 6.29) * mm, "end": v(-22.58, 8.2) * mm});
            skLineSegment(sketch, "E33.1.0.37", {"start": v(-13.36, 17.08) * mm, "end": v(-14.96, 18.99) * mm});
            skLineSegment(sketch, "E33.1.0.38", {"start": v(-11, 13.59) * mm, "end": v(-14.3, 13.59) * mm});
            skLineSegment(sketch, "E33.1.0.39", {"start": v(-22.58, 8.2) * mm, "end": v(-25.88, 8.2) * mm});
            skLineSegment(sketch, "E33.1.0.40", {"start": v(-21.13, 13.59) * mm, "end": v(-24.43, 13.59) * mm});
            skLineSegment(sketch, "E33.1.0.41", {"start": v(-26.33, 8.49) * mm, "end": v(-25.28, 12.38) * mm});
            skLineSegment(sketch, "E33.1.0.42", {"start": v(-15.41, 18.74) * mm, "end": v(-13.92, 16.96) * mm});
            skLineSegment(sketch, "E33.1.0.43", {"start": v(-11, 6.29) * mm, "end": v(-12.44, 8.2) * mm});
            skLineSegment(sketch, "E33.1.0.44", {"start": v(-18.68, 6.54) * mm, "end": v(-16.19, 8.49) * mm});
            skLineSegment(sketch, "E33.1.0.45", {"start": v(-23.5, 17.08) * mm, "end": v(-25.1, 18.99) * mm});
            skLineSegment(sketch, "E33.1.0.46", {"start": v(-21.64, 11.68) * mm, "end": v(-21.13, 13.59) * mm});
            skLineSegment(sketch, "E33.1.0.47", {"start": v(-11.5, 11.68) * mm, "end": v(-11, 13.59) * mm});
            skLineSegment(sketch, "E33.1.0.48", {"start": v(-24.43, 13.59) * mm, "end": v(-24.94, 11.68) * mm});
            skLineSegment(sketch, "E33.1.0.49", {"start": v(-20.93, 12.38) * mm, "end": v(-18.96, 12.38) * mm});
            skLineSegment(sketch, "E33.1.0.50", {"start": v(-15, 12.9) * mm, "end": v(-16.98, 12.9) * mm});
            skLineSegment(sketch, "E33.1.0.51", {"start": v(-15.14, 12.38) * mm, "end": v(-17.12, 12.38) * mm});
            skLineSegment(sketch, "E33.1.0.52", {"start": v(-25.15, 12.9) * mm, "end": v(-27.12, 12.9) * mm});
            skLineSegment(sketch, "E33.1.0.53", {"start": v(-14.3, 13.59) * mm, "end": v(-14.8, 11.68) * mm});
            skLineSegment(sketch, "E33.1.0.54", {"start": v(-19.69, 18.99) * mm, "end": v(-20.2, 17.08) * mm});
            skLineSegment(sketch, "E33.1.0.55", {"start": v(-19.16, 18.99) * mm, "end": v(-17.19, 18.99) * mm});
            skLineSegment(sketch, "E33.direction1", {"start": v(7.25, 6.54) * mm, "end": v(-28.82, 6.54) * mm, "construction": true});
            skLineSegment(sketch, "E34.bottom", {"start": v(-23.17, -33.34) * mm, "end": v(25.64, -33.34) * mm});
            skLineSegment(sketch, "E34.top", {"start": v(-23.17, -35.24) * mm, "end": v(25.64, -35.24) * mm});
            skLineSegment(sketch, "E34.left", {"start": v(-23.17, -33.34) * mm, "end": v(-23.17, -35.24) * mm});
            skLineSegment(sketch, "E34.right", {"start": v(25.64, -33.34) * mm, "end": v(25.64, -35.24) * mm});
            skLineSegment(sketch, "E35.bottom", {"start": v(-23.17, -13.9) * mm, "end": v(25.64, -13.9) * mm});
            skLineSegment(sketch, "E35.top", {"start": v(-23.17, -15.81) * mm, "end": v(25.64, -15.81) * mm});
            skLineSegment(sketch, "E35.left", {"start": v(-23.17, -13.9) * mm, "end": v(-23.17, -15.81) * mm});
            skLineSegment(sketch, "E35.right", {"start": v(25.64, -13.9) * mm, "end": v(25.64, -15.81) * mm});
            skLineSegment(sketch, "E36.bottom", {"start": v(-29.27, -44.32) * mm, "end": v(-25.84, -44.32) * mm});
            skLineSegment(sketch, "E36.top", {"start": v(-29.27, -46.23) * mm, "end": v(-22.42, -46.23) * mm});
            skLineSegment(sketch, "E36.left", {"start": v(-29.27, -44.32) * mm, "end": v(-29.27, -46.23) * mm});
            skLineSegment(sketch, "E36.right", {"start": v(-22.42, -44.32) * mm, "end": v(-22.42, -45.28) * mm});
            skLineSegment(sketch, "E37.bottom", {"start": v(-26.8, -41.21) * mm, "end": v(-24.9, -41.21) * mm});
            skLineSegment(sketch, "E37.top", {"start": v(-26.8, -43.82) * mm, "end": v(-25.84, -43.82) * mm});
            skLineSegment(sketch, "E37.left", {"start": v(-26.8, -41.21) * mm, "end": v(-26.8, -43.82) * mm});
            skLineSegment(sketch, "E37.right", {"start": v(-24.9, -41.21) * mm, "end": v(-24.9, -43.82) * mm});
            skLineSegment(sketch, "E38.bottom", {"start": v(-26.8, -46.74) * mm, "end": v(-24.9, -46.74) * mm});
            skLineSegment(sketch, "E38.top", {"start": v(-26.8, -49.34) * mm, "end": v(-24.9, -49.34) * mm});
            skLineSegment(sketch, "E38.left", {"start": v(-26.8, -46.74) * mm, "end": v(-26.8, -49.34) * mm});
            skLineSegment(sketch, "E38.right", {"start": v(-24.9, -46.74) * mm, "end": v(-24.9, -49.34) * mm});
            skLineSegment(sketch, "E39", {"start": v(-19.04, -45.28) * mm, "end": v(-19.3, -46.23) * mm});
            skLineSegment(sketch, "E40", {"start": v(-22.42, -45.28) * mm, "end": v(-22.42, -46.23) * mm});
            skLineSegment(sketch, "E41", {"start": v(-25.84, -43.82) * mm, "end": v(-24.9, -43.82) * mm});
            skLineSegment(sketch, "E42", {"start": v(-25.84, -44.32) * mm, "end": v(-22.42, -44.32) * mm});
            skLineSegment(sketch, "E43.bottom", {"start": v(-23.17, 5.14) * mm, "end": v(25.64, 5.14) * mm});
            skLineSegment(sketch, "E43.top", {"start": v(-23.17, 3.24) * mm, "end": v(25.64, 3.24) * mm});
            skLineSegment(sketch, "E43.left", {"start": v(-23.17, 5.14) * mm, "end": v(-23.17, 3.24) * mm});
            skLineSegment(sketch, "E43.right", {"start": v(25.64, 5.14) * mm, "end": v(25.64, 3.24) * mm});
            skLineSegment(sketch, "E44.bottom", {"start": v(29.43, 27.11) * mm, "end": v(6.57, 27.11) * mm});
            skLineSegment(sketch, "E44.top", {"start": v(29.43, 20.51) * mm, "end": v(6.57, 20.51) * mm});
            skLineSegment(sketch, "E44.left", {"start": v(29.43, 27.11) * mm, "end": v(29.43, 20.51) * mm});
            skLineSegment(sketch, "E44.right", {"start": v(6.57, 27.11) * mm, "end": v(6.57, 20.51) * mm});
            skPoint(sketch, "E45.firstSnap0", {"position": v(29.43, 23.81) * mm});
            skLineSegment(sketch, "E45.bottom", {"start": v(29.43, 51.24) * mm, "end": v(6.57, 51.24) * mm});
            skLineSegment(sketch, "E45.top", {"start": v(29.43, 44.64) * mm, "end": v(6.57, 44.64) * mm});
            skLineSegment(sketch, "E45.left", {"start": v(29.43, 51.24) * mm, "end": v(29.43, 44.64) * mm});
            skLineSegment(sketch, "E45.right", {"start": v(6.57, 51.24) * mm, "end": v(6.57, 44.64) * mm});
            skLineSegment(sketch, "E46.bottom", {"start": v(-6.64, 27.11) * mm, "end": v(-29.5, 27.11) * mm});
            skLineSegment(sketch, "E46.top", {"start": v(-6.64, 20.51) * mm, "end": v(-29.5, 20.51) * mm});
            skLineSegment(sketch, "E46.left", {"start": v(-6.64, 27.11) * mm, "end": v(-6.64, 20.51) * mm});
            skLineSegment(sketch, "E46.right", {"start": v(-29.5, 27.11) * mm, "end": v(-29.5, 20.51) * mm});
            skLineSegment(sketch, "E47.bottom", {"start": v(-6.64, 51.24) * mm, "end": v(-29.5, 51.24) * mm});
            skLineSegment(sketch, "E47.top", {"start": v(-6.64, 30.42) * mm, "end": v(-29.5, 30.42) * mm});
            skLineSegment(sketch, "E47.left", {"start": v(-6.64, 51.24) * mm, "end": v(-6.64, 30.42) * mm});
            skLineSegment(sketch, "E47.right", {"start": v(-29.5, 51.24) * mm, "end": v(-29.5, 30.42) * mm});
            skLineSegment(sketch, "E48.0.1.0", {"start": v(-25.84, -24.9) * mm, "end": v(-22.42, -24.9) * mm});
            skLineSegment(sketch, "E48.0.1.1", {"start": v(-29.27, -24.9) * mm, "end": v(-25.84, -24.9) * mm});
            skLineSegment(sketch, "E48.0.1.2", {"start": v(-26.8, -21.78) * mm, "end": v(-26.8, -24.38) * mm});
            skLineSegment(sketch, "E48.0.1.3", {"start": v(-26.8, -21.78) * mm, "end": v(-24.9, -21.78) * mm});
            skLineSegment(sketch, "E48.0.1.4", {"start": v(-24.9, -21.78) * mm, "end": v(-24.9, -24.38) * mm});
            skLineSegment(sketch, "E48.0.1.5", {"start": v(-24.9, -27.3) * mm, "end": v(-24.9, -29.9) * mm});
            skLineSegment(sketch, "E48.0.1.6", {"start": v(-26.8, -29.9) * mm, "end": v(-24.9, -29.9) * mm});
            skLineSegment(sketch, "E48.0.1.7", {"start": v(-26.8, -27.3) * mm, "end": v(-26.8, -29.9) * mm});
            skLineSegment(sketch, "E48.0.1.8", {"start": v(-26.8, -27.3) * mm, "end": v(-24.9, -27.3) * mm});
            skLineSegment(sketch, "E48.0.1.9", {"start": v(-29.27, -24.9) * mm, "end": v(-29.27, -26.8) * mm});
            skLineSegment(sketch, "E48.0.1.10", {"start": v(-29.27, -26.8) * mm, "end": v(-22.42, -26.8) * mm});
            skLineSegment(sketch, "E48.0.1.11", {"start": v(-26.8, -24.38) * mm, "end": v(-25.84, -24.38) * mm});
            skLineSegment(sketch, "E48.0.1.12", {"start": v(-22.42, -24.9) * mm, "end": v(-22.42, -25.84) * mm});
            skLineSegment(sketch, "E48.0.1.13", {"start": v(-22.42, -25.84) * mm, "end": v(-22.42, -26.8) * mm});
            skLineSegment(sketch, "E48.0.1.14", {"start": v(-25.84, -24.38) * mm, "end": v(-24.9, -24.38) * mm});
            skLineSegment(sketch, "E48.0.2.0", {"start": v(-25.84, -5.46) * mm, "end": v(-22.42, -5.46) * mm});
            skLineSegment(sketch, "E48.0.2.1", {"start": v(-29.27, -5.46) * mm, "end": v(-25.84, -5.46) * mm});
            skLineSegment(sketch, "E48.0.2.2", {"start": v(-26.8, -2.35) * mm, "end": v(-26.8, -4.95) * mm});
            skLineSegment(sketch, "E48.0.2.3", {"start": v(-26.8, -2.35) * mm, "end": v(-24.9, -2.35) * mm});
            skLineSegment(sketch, "E48.0.2.4", {"start": v(-24.9, -2.35) * mm, "end": v(-24.9, -4.95) * mm});
            skLineSegment(sketch, "E48.0.2.5", {"start": v(-24.9, -7.87) * mm, "end": v(-24.9, -10.48) * mm});
            skLineSegment(sketch, "E48.0.2.6", {"start": v(-26.8, -10.48) * mm, "end": v(-24.9, -10.48) * mm});
            skLineSegment(sketch, "E48.0.2.7", {"start": v(-26.8, -7.87) * mm, "end": v(-26.8, -10.48) * mm});
            skLineSegment(sketch, "E48.0.2.8", {"start": v(-26.8, -7.87) * mm, "end": v(-24.9, -7.87) * mm});
            skLineSegment(sketch, "E48.0.2.9", {"start": v(-29.27, -5.46) * mm, "end": v(-29.27, -7.37) * mm});
            skLineSegment(sketch, "E48.0.2.10", {"start": v(-29.27, -7.37) * mm, "end": v(-22.42, -7.37) * mm});
            skLineSegment(sketch, "E48.0.2.11", {"start": v(-26.8, -4.95) * mm, "end": v(-25.84, -4.95) * mm});
            skLineSegment(sketch, "E48.0.2.12", {"start": v(-22.42, -5.46) * mm, "end": v(-22.42, -6.41) * mm});
            skLineSegment(sketch, "E48.0.2.13", {"start": v(-22.42, -6.41) * mm, "end": v(-22.42, -7.37) * mm});
            skLineSegment(sketch, "E48.0.2.14", {"start": v(-25.84, -4.95) * mm, "end": v(-24.9, -4.95) * mm});
            skLineSegment(sketch, "E48.direction1", {"start": v(-26.8, -49.34) * mm, "end": v(-1.4, -49.34) * mm, "construction": true});
            skLineSegment(sketch, "E48.direction2", {"start": v(-26.8, -49.34) * mm, "end": v(-26.8, -29.9) * mm, "construction": true});
            skPoint(sketch, "E49.visualSharp", {"position": v(-31.75, 54.6) * mm});
            skPoint(sketch, "E50.visualSharp", {"position": v(31.75, 54.6) * mm});
            skPoint(sketch, "E51.visualSharp", {"position": v(31.75, -54.61) * mm});
            skPoint(sketch, "E52.visualSharp", {"position": v(-31.75, -54.61) * mm});
            skSolve(sketch);
        }
        {
            var Q0;
            Q0=qSketchRegion(id+"F2",true);
            extrude(context, id + "F3", {"entities" : qUnion([Q0]), "operationType" : NewBodyOperationType.REMOVE, "endBound" : BoundingType.THROUGH_ALL, "oppositeDirection" : true, "depth" : 25.4 * mm});
        }
        {
            var Q0;
            Q0=makeQuery(id+"F1.opExtrude","SWEPT_EDGE",EDGE,{"disambiguationData":[OSD([sQuery(id+"F0.wireOp",EDGE,"E0.top"),sQuery(id+"F0.wireOp",EDGE,"E0.right")])]});
            var Q1;
            Q1=makeQuery(id+"F1.opExtrude","SWEPT_EDGE",EDGE,{"disambiguationData":[OSD([sQuery(id+"F0.wireOp",EDGE,"E0.top"),sQuery(id+"F0.wireOp",EDGE,"E0.left")])]});
            var Q2;
            Q2=makeQuery(id+"F1.opExtrude","SWEPT_EDGE",EDGE,{"disambiguationData":[OSD([sQuery(id+"F0.wireOp",EDGE,"E0.bottom"),sQuery(id+"F0.wireOp",EDGE,"E0.left")])]});
            var Q3;
            Q3=makeQuery(id+"F1.opExtrude","SWEPT_EDGE",EDGE,{"disambiguationData":[OSD([sQuery(id+"F0.wireOp",EDGE,"E0.bottom"),sQuery(id+"F0.wireOp",EDGE,"E0.right")])]});
            fillet(context, id + "F4", {"entities" : qUnion([Q0, Q1, Q2, Q3]), "radius" : 2.54 * mm, "tangentPropagation" : true, "allowEdgeOverflow" : false});
        }
    });
